# Revit family: CAF_DWDI_CW_DBD
name_source: partatom
category: Mechanical Equipment
units: mm (PartAtom-declared; Revit-internal decimal feet)

## family parameters
Always vertical = Yes
Cut with Voids When Loaded = No
Part Type = Normal
Room Calculation Point = No
Round Connector Dimension = Use Radius
Shared = No
Work Plane-Based = No

## types (58) — shared parameters
0 = 0"
1" = 1"
1.5 = 1 1/2"
2" = 2"
2' = 24"
3" = 3"
60 = 60.00°
Manufacturer = Loren Cook Company
Model = CAF-DWDI
ONE EIGTH = 1/8"
PLAY = 2"
URL = www.lorencook.com

## per-type parameters (varying)
- 120_CAF-DWDI_CW_DBD_CLASS_1: ((M+U+U+N+N)-((B+.25")/2))/2=3"; (A+.25")/2=6 3/16"; (B+.25")/2=8 31/32"; (D-(A+.25"))/2=15/16"; (INLET/2)+1.5"=9 1/2"; (INLET/2)+1.625"=9 9/16"; (INLET/2)-.125"=7 15/16"; (M-(B+.25")/2=1 7/16"; -(B+.25")/2=-8 31/32"; -P=-26 11/16"; A=12 1/8"; A+.25"=12 3/8"; A/2=6 1/16"; B=17 11/16"; B+.25"=17 15/16"; B/2=8 27/32"; BOTTOM=5 7/32"; C=1 7/16"; C+C=2 7/8"; C/2=23/32"; D/2=7 1/8"; D/7=1 3/16"; DB_D=20 1/16"; DB_E=9 13/16"; DB_F=23 3/8"; DB_G=9 5/8"; DB_H=1 1/16"; DB_J=23 3/8"; DB_R=11/16"; E/2=9 29/32"; G+(INLET/2)+1.625"=19 3/8"; G-(INLET/2)-1.625"=1/4"; G-(R/2)=3/16"; H-J=9 5/8"; INLET=16 1/8"; INLET/2=8 1/16"; INLET/4=4 1/32"; K=9/16"; K/2=9/32"; L=10 7/16"; M=20 13/16"; N=2 3/4"; OLD_G=9 13/16"; OLD_R=19 1/4"; OLD_R/2=9 5/8"; P=26 11/16"; S=20 1/2"; S/2=10 1/4"; T=19 1/2"; T/2=9 3/4"; Type Comments=Centrifugal Airfoil Blower Clockwise Down Blast Arrangement 3 Low Profile Class 1; U=4 5/16"; U-N=1 9/16"; V=1"; V+(D-(A+.25"))/2=1 15/16"
- 135_CAF-DWDI_CW_DBD_CLASS_1: ((M+U+U+N+N)-((B+.25")/2))/2=3"; (A+.25")/2=6 15/16"; (B+.25")/2=10 3/32"; (D-(A+.25"))/2=15/16"; (INLET/2)+1.5"=10 1/4"; (INLET/2)+1.625"=10 5/16"; (INLET/2)-.125"=8 11/16"; (M-(B+.25")/2=1 7/16"; -(B+.25")/2=-10 3/32"; -P=-28 15/16"; A=13 5/8"; A+.25"=13 7/8"; A/2=6 13/16"; B=19 15/16"; B+.25"=20 3/16"; B/2=9 31/32"; BOTTOM=5 7/8"; C=1 7/16"; C+C=2 7/8"; C/2=23/32"; D/2=7 7/8"; D/7=1 5/16"; DB_D=22 9/16"; DB_E=10 13/16"; DB_F=25 7/8"; DB_G=10 1/2"; DB_H=1 1/16"; DB_J=25 7/8"; DB_R=11/16"; E/2=11 1/32"; G+(INLET/2)+1.625"=21 1/8"; G-(INLET/2)-1.625"=1/2"; G-(R/2)=5/16"; H-J=10 13/16"; INLET=17 5/8"; INLET/2=8 13/16"; INLET/4=4 13/32"; K=9/16"; K/2=9/32"; L=11 9/16"; M=23 1/16"; N=2 3/4"; OLD_G=10 13/16"; OLD_R=21"; OLD_R/2=10 1/2"; P=28 15/16"; S=23"; S/2=11 1/2"; T=21 3/4"; T/2=10 7/8"; Type Comments=Centrifugal Airfoil Blower Clockwise Down Blast Arrangement 3 Low Profile Class 1; U=4 5/16"; U-N=1 9/16"; V=1"; V+(D-(A+.25"))/2=1 15/16"
- 150_CAF-DWDI_CW_DBD_CLASS_1: ((M+U+U+N+N)-((B+.25")/2))/2=3"; (A+.25")/2=7 3/4"; (B+.25")/2=11 1/8"; (D-(A+.25"))/2=15/16"; (INLET/2)+1.5"=11"; (INLET/2)+1.625"=11 1/16"; (INLET/2)-.125"=9 7/16"; (M-(B+.25")/2=1 15/16"; -(B+.25")/2=-11 1/8"; -P=-31 5/8"; A=15 1/4"; A+.25"=15 1/2"; A/2=7 5/8"; B=22"; B+.25"=22 1/4"; B/2=11"; BOTTOM=6 17/32"; C=1 7/16"; C+C=2 7/8"; C/2=23/32"; D/2=8 11/16"; D/7=1 7/16"; DB_D=25 1/16"; DB_E=12"; DB_F=28 7/16"; DB_G=11 1/2"; DB_H=1 1/16"; DB_J=28 3/16"; DB_R=7/8"; E/2=12 1/16"; G+(INLET/2)+1.625"=23 1/16"; G-(INLET/2)-1.625"=15/16"; G-(R/2)=3/4"; H-J=12"; INLET=19 1/8"; INLET/2=9 9/16"; INLET/4=4 25/32"; K=9/16"; K/2=9/32"; L=13 1/16"; M=26 1/8"; N=3 3/8"; OLD_G=12"; OLD_R=22 1/2"; OLD_R/2=11 1/4"; P=31 5/8"; S=24 15/16"; S/2=12 15/32"; T=24 3/8"; T/2=12 3/16"; Type Comments=Centrifugal Airfoil Blower Clockwise Down Blast Arrangement 3 Low Profile Class 1; U=4 7/16"; U-N=1 1/16"; V=1"; V+(D-(A+.25"))/2=1 15/16"
- 165_CAF-DWDI_CW_DBD_CLASS_1: ((M+U+U+N+N)-((B+.25")/2))/2=3"; (A+.25")/2=8 19/32"; (B+.25")/2=12 1/8"; (D-(A+.25"))/2=15/16"; (INLET/2)+1.5"=12 1/32"; (INLET/2)+1.625"=12 3/32"; (INLET/2)-.125"=10 15/32"; (M-(B+.25")/2=1 15/16"; -(B+.25")/2=-12 1/8"; -P=-33 11/16"; A=16 15/16"; A+.25"=17 3/16"; A/2=8 15/32"; B=24"; B+.25"=24 1/4"; B/2=12"; BOTTOM=7 3/16"; C=1 11/16"; C+C=3 3/8"; C/2=27/32"; D/2=9 17/32"; D/7=1 19/32"; DB_D=27 1/2"; DB_E=13 1/8"; DB_F=31 3/16"; DB_G=12 11/16"; DB_H=1 1/16"; DB_J=30 5/8"; DB_R=7/8"; E/2=13 1/16"; G+(INLET/2)+1.625"=25 7/32"; G-(INLET/2)-1.625"=1 1/32"; G-(R/2)=1"; H-J=13 1/8"; INLET=21 3/16"; INLET/2=10 19/32"; INLET/4=5 5/16"; K=15/16"; K/2=15/32"; L=14 1/16"; M=28 1/8"; N=3 3/8"; OLD_G=13 1/8"; OLD_R=24 1/4"; OLD_R/2=12 1/8"; P=33 11/16"; S=27 3/8"; S/2=13 11/16"; T=26 3/8"; T/2=13 3/16"; Type Comments=Centrifugal Airfoil Blower Clockwise Down Blast Arrangement 3 Low Profile Class 1; U=4 7/16"; U-N=1 1/16"; V=1"; V+(D-(A+.25"))/2=1 15/16"
- 180_CAF-DWDI_CW_DBD_CLASS_1: ((M+U+U+N+N)-((B+.25")/2))/2=3"; (A+.25")/2=9 3/8"; (B+.25")/2=13 5/32"; (D-(A+.25"))/2=15/16"; (INLET/2)+1.5"=12 25/32"; (INLET/2)+1.625"=12 27/32"; (INLET/2)-.125"=11 7/32"; (M-(B+.25")/2=1 15/16"; -(B+.25")/2=-13 5/32"; -P=-36 1/8"; A=18 1/2"; A+.25"=18 3/4"; A/2=9 1/4"; B=26 1/16"; B+.25"=26 5/16"; B/2=13 1/32"; BOTTOM=7 27/32"; C=1 11/16"; C+C=3 3/8"; C/2=27/32"; D/2=10 5/16"; D/7=1 23/32"; DB_D=30"; DB_E=14 5/16"; DB_F=33 15/16"; DB_G=13 13/16"; DB_H=1 1/16"; DB_J=33 1/2"; DB_R=7/8"; E/2=14 3/32"; G+(INLET/2)+1.625"=27 5/32"; G-(INLET/2)-1.625"=1 15/32"; G-(R/2)=15/16"; H-J=14 5/16"; INLET=22 11/16"; INLET/2=11 11/32"; INLET/4=5 11/16"; K=15/16"; K/2=15/32"; L=15 1/8"; M=30 3/16"; N=3 3/4"; OLD_G=14 5/16"; OLD_R=26 3/4"; OLD_R/2=13 3/8"; P=36 1/8"; S=29 3/4"; S/2=14 7/8"; T=28 7/16"; T/2=14 7/32"; Type Comments=Centrifugal Airfoil Blower Clockwise Down Blast Arrangement 3 Low Profile Class 1; U=4 13/16"; U-N=1 1/16"; V=1"; V+(D-(A+.25"))/2=1 15/16"
- 195_CAF-DWDI_CW_DBD_CLASS_1: ((M+U+U+N+N)-((B+.25")/2))/2=3"; (A+.25")/2=9 7/8"; (B+.25")/2=14 11/32"; (D-(A+.25"))/2=31/32"; (INLET/2)+1.5"=13 17/32"; (INLET/2)+1.625"=13 19/32"; (INLET/2)-.125"=11 31/32"; (M-(B+.25")/2=1 15/16"; -(B+.25")/2=-14 11/32"; -P=-38 1/2"; A=19 1/2"; A+.25"=19 3/4"; A/2=9 3/4"; B=28 7/16"; B+.25"=28 11/16"; B/2=14 7/32"; BOTTOM=8 15/32"; C=1 11/16"; C+C=3 3/8"; C/2=27/32"; D/2=10 27/32"; D/7=1 13/16"; DB_D=32 7/16"; DB_E=15 1/2"; DB_F=36 5/8"; DB_G=14 15/16"; DB_H=1 1/16"; DB_J=35 15/16"; DB_R=7/8"; E/2=15 5/16"; G+(INLET/2)+1.625"=29 3/32"; G-(INLET/2)-1.625"=1 29/32"; G-(R/2)=1 1/4"; H-J=15 1/2"; INLET=24 3/16"; INLET/2=12 3/32"; INLET/4=6 1/16"; K=15/16"; K/2=15/32"; L=16 5/16"; M=32 9/16"; N=3 3/4"; OLD_G=15 1/2"; OLD_R=28 1/2"; OLD_R/2=14 1/4"; P=38 1/2"; S=32 3/16"; S/2=16 3/32"; T=30 13/16"; T/2=15 13/32"; Type Comments=Centrifugal Airfoil Blower Clockwise Down Blast Arrangement 3 Low Profile Class 1; U=4 13/16"; U-N=1 1/16"; V=1"; V+(D-(A+.25"))/2=1 31/32"
- 210_CAF-DWDI_CW_DBD_CLASS_1: ((M+U+U+N+N)-((B+.25")/2))/2=4"; (A+.25")/2=10 15/16"; (B+.25")/2=15 5/16"; (D-(A+.25"))/2=31/32"; (INLET/2)+1.5"=14 13/32"; (INLET/2)+1.625"=14 15/32"; (INLET/2)-.125"=12 27/32"; (M-(B+.25")/2=1 15/16"; -(B+.25")/2=-15 5/16"; -P=-41 7/16"; A=21 5/8"; A+.25"=21 7/8"; A/2=10 13/16"; B=30 3/8"; B+.25"=30 5/8"; B/2=15 3/16"; BOTTOM=9 1/8"; C=1 11/16"; C+C=3 3/8"; C/2=27/32"; D/2=11 29/32"; D/7=2"; DB_D=34 15/16"; DB_E=16 11/16"; DB_F=39 3/8"; DB_G=16 1/8"; DB_H=1 1/16"; DB_J=38 5/16"; DB_R=7/8"; E/2=16 9/32"; G+(INLET/2)+1.625"=31 5/32"; G-(INLET/2)-1.625"=2 7/32"; G-(R/2)=1 11/16"; H-J=16 11/16"; INLET=25 15/16"; INLET/2=12 31/32"; INLET/4=6 1/2"; K=15/16"; K/2=15/32"; L=17 1/4"; M=34 1/2"; N=3 3/4"; OLD_G=16 11/16"; OLD_R=30"; OLD_R/2=15"; P=41 7/16"; S=34 9/16"; S/2=17 9/32"; T=32 3/4"; T/2=16 3/8"; Type Comments=Centrifugal Airfoil Blower Clockwise Down Blast Arrangement 3 Low Profile Class 1; U=5 13/16"; U-N=2 1/16"; V=1"; V+(D-(A+.25"))/2=1 31/32"
- 225_CAF-DWDI_CW_DBD_CLASS_1: ((M+U+U+N+N)-((B+.25")/2))/2=4"; (A+.25")/2=11 23/32"; (B+.25")/2=16 3/8"; (D-(A+.25"))/2=1 15/32"; (INLET/2)+1.5"=15 5/32"; (INLET/2)+1.625"=15 7/32"; (INLET/2)-.125"=13 19/32"; (M-(B+.25")/2=1 15/16"; -(B+.25")/2=-16 3/8"; -P=-44 1/16"; A=23 3/16"; A+.25"=23 7/16"; A/2=11 19/32"; B=32 1/2"; B+.25"=32 3/4"; B/2=16 1/4"; BOTTOM=9 25/32"; C=1 15/16"; C+C=3 7/8"; C/2=31/32"; D/2=13 3/16"; D/7=2 3/16"; DB_D=37 3/8"; DB_E=17 13/16"; DB_F=42 5/8"; DB_G=17 1/4"; DB_H=1 9/16"; DB_J=41 1/4"; DB_R=7/8"; E/2=17 27/32"; G+(INLET/2)+1.625"=33 1/32"; G-(INLET/2)-1.625"=2 19/32"; G-(R/2)=1 15/16"; H-J=17 13/16"; INLET=27 7/16"; INLET/2=13 23/32"; INLET/4=6 7/8"; K=15/16"; K/2=15/32"; L=18 5/16"; M=36 5/8"; N=4 1/4"; OLD_G=17 13/16"; OLD_R=31 3/4"; OLD_R/2=15 7/8"; P=44 1/16"; S=37 1/2"; S/2=18 3/4"; T=34 7/8"; T/2=17 7/16"; Type Comments=Centrifugal Airfoil Blower Clockwise Down Blast Arrangement 3 Low Profile Class 1; U=6 5/16"; U-N=2 1/16"; V=1"; V+(D-(A+.25"))/2=2 15/32"
- 245_CAF-DWDI_CW_DBD_CLASS_1: ((M+U+U+N+N)-((B+.25")/2))/2=4"; (A+.25")/2=12 7/8"; (B+.25")/2=17 21/32"; (D-(A+.25"))/2=1 15/32"; (INLET/2)+1.5"=16 5/32"; (INLET/2)+1.625"=16 7/32"; (INLET/2)-.125"=14 19/32"; (M-(B+.25")/2=1 15/16"; -(B+.25")/2=-17 21/32"; -P=-46 5/8"; A=25 1/2"; A+.25"=25 3/4"; A/2=12 3/4"; B=35 1/16"; B+.25"=35 5/16"; B/2=17 17/32"; BOTTOM=10 21/32"; C=1 15/16"; C+C=3 7/8"; C/2=31/32"; D/2=14 11/32"; D/7=2 13/32"; DB_D=40 11/16"; DB_E=19 3/8"; DB_F=46 1/4"; DB_G=18 3/4"; DB_H=1 9/16"; DB_J=44 3/8"; DB_R=7/8"; E/2=19 1/8"; G+(INLET/2)+1.625"=35 19/32"; G-(INLET/2)-1.625"=3 5/32"; G-(R/2)=2 1/2"; H-J=19 3/8"; INLET=29 7/16"; INLET/2=14 23/32"; INLET/4=7 3/8"; K=15/16"; K/2=15/32"; L=19 5/8"; M=39 3/16"; N=4 1/4"; OLD_G=19 3/8"; OLD_R=33 3/4"; OLD_R/2=16 7/8"; P=46 5/8"; S=40 5/8"; S/2=20 5/16"; T=37 7/16"; T/2=18 23/32"; Type Comments=Centrifugal Airfoil Blower Clockwise Down Blast Arrangement 3 Low Profile Class 1; U=6 5/16"; U-N=2 1/16"; V=1"; V+(D-(A+.25"))/2=2 15/32"
- 270_CAF-DWDI_CW_DBD_CLASS_1: ((M+U+U+N+N)-((B+.25")/2))/2=4 1/2"; (A+.25")/2=13 7/8"; (B+.25")/2=19 27/32"; (D-(A+.25"))/2=1 15/32"; (INLET/2)+1.5"=17 13/32"; (INLET/2)+1.625"=17 15/32"; (INLET/2)-.125"=15 27/32"; (M-(B+.25")/2=2 7/16"; -(B+.25")/2=-19 27/32"; -P=-51 1/2"; A=27 1/2"; A+.25"=27 3/4"; A/2=13 3/4"; B=39 7/16"; B+.25"=39 11/16"; B/2=19 23/32"; BOTTOM=11 3/4"; C=2 3/16"; C+C=4 3/8"; C/2=1 3/32"; D/2=15 11/32"; D/7=2 9/16"; DB_D=44 13/16"; DB_E=21 5/16"; DB_F=50 13/16"; DB_G=20 11/16"; DB_H=1 9/16"; DB_J=48 7/8"; DB_R=1 1/8"; E/2=21 5/16"; G+(INLET/2)+1.625"=38 25/32"; G-(INLET/2)-1.625"=3 27/32"; G-(R/2)=2 9/16"; H-J=21 5/16"; INLET=31 15/16"; INLET/2=15 31/32"; INLET/4=8"; K=15/16"; K/2=15/32"; L=22 5/16"; M=44 9/16"; N=4 1/4"; OLD_G=21 5/16"; OLD_R=37 1/2"; OLD_R/2=18 3/4"; P=51 1/2"; S=44 1/8"; S/2=22 1/16"; T=42 5/16"; T/2=21 5/32"; Type Comments=Centrifugal Airfoil Blower Clockwise Down Blast Arrangement 3 Low Profile Class 1; U=6 5/16"; U-N=2 1/16"; V=1"; V+(D-(A+.25"))/2=2 15/32"
- 300_CAF-DWDI_CW_DBD_CLASS_1: ((M+U+U+N+N)-((B+.25")/2))/2=4 9/16"; (A+.25")/2=15 23/32"; (B+.25")/2=21 5/8"; (D-(A+.25"))/2=1 15/32"; (INLET/2)+1.5"=18 29/32"; (INLET/2)+1.625"=18 31/32"; (INLET/2)-.125"=17 11/32"; (M-(B+.25")/2=2 7/16"; -(B+.25")/2=-21 5/8"; -P=-55 1/8"; A=31 3/16"; A+.25"=31 7/16"; A/2=15 19/32"; B=43"; B+.25"=43 1/4"; B/2=21 1/2"; BOTTOM=13 1/32"; C=2 3/16"; C+C=4 3/8"; C/2=1 3/32"; D/2=17 3/16"; D/7=2 7/8"; DB_D=49 3/4"; DB_E=23 11/16"; DB_F=56 1/4"; DB_G=22 15/16"; DB_H=1 9/16"; DB_J=53 9/16"; DB_R=1 1/8"; E/2=23 3/32"; G+(INLET/2)+1.625"=42 21/32"; G-(INLET/2)-1.625"=4 23/32"; G-(R/2)=3 7/16"; H-J=23 11/16"; INLET=34 15/16"; INLET/2=17 15/32"; INLET/4=8 3/4"; K=15/16"; K/2=15/32"; L=24 1/16"; M=48 1/8"; N=4 1/4"; OLD_G=23 11/16"; OLD_R=40 1/2"; OLD_R/2=20 1/4"; P=55 1/8"; S=48 13/16"; S/2=24 13/32"; T=45 7/8"; T/2=22 15/16"; Type Comments=Centrifugal Airfoil Blower Clockwise Down Blast Arrangement 3 Low Profile Class 1; U=6 3/8"; U-N=2 1/8"; V=1"; V+(D-(A+.25"))/2=2 15/32"
- 330_CAF-DWDI_CW_DBD_CLASS_1: ((M+U+U+N+N)-((B+.25")/2))/2=4 9/16"; (A+.25")/2=17 3/8"; (B+.25")/2=23 21/32"; (D-(A+.25"))/2=2"; (INLET/2)+1.5"=20 13/32"; (INLET/2)+1.625"=20 15/32"; (INLET/2)-.125"=18 27/32"; (M-(B+.25")/2=2 15/16"; -(B+.25")/2=-23 21/32"; -P=-59 5/16"; A=34 1/2"; A+.25"=34 3/4"; A/2=17 1/4"; B=47 1/16"; B+.25"=47 5/16"; B/2=23 17/32"; BOTTOM=14 11/32"; C=2 7/16"; C+C=4 7/8"; C/2=1 7/32"; D/2=19 3/8"; D/7=3 7/32"; DB_D=54 11/16"; DB_E=26"; DB_F=62 1/4"; DB_G=25 1/4"; DB_H=2 1/16"; DB_J=57 13/16"; DB_R=1 5/16"; E/2=25 21/32"; G+(INLET/2)+1.625"=46 15/32"; G-(INLET/2)-1.625"=5 17/32"; G-(R/2)=5 7/32"; H-J=26"; INLET=37 15/16"; INLET/2=18 31/32"; INLET/4=9 1/2"; K=15/16"; K/2=15/32"; L=26 5/8"; M=53 3/16"; N=4 3/8"; OLD_G=26"; OLD_R=41 9/16"; OLD_R/2=20 25/32"; P=59 5/16"; S=53 3/4"; S/2=26 7/8"; T=50 9/16"; T/2=25 9/32"; Type Comments=Centrifugal Airfoil Blower Clockwise Down Blast Arrangement 3 Low Profile Class 1; U=6"; U-N=1 5/8"; V=1"; V+(D-(A+.25"))/2=3"
- 365_CAF-DWDI_CW_DBD_CLASS_1: ((M+U+U+N+N)-((B+.25")/2))/2=5 1/16"; (A+.25")/2=19 15/32"; (B+.25")/2=26 7/32"; (D-(A+.25"))/2=2"; (INLET/2)+1.5"=22 5/32"; (INLET/2)+1.625"=22 7/32"; (INLET/2)-.125"=20 19/32"; (M-(B+.25")/2=2 15/16"; -(B+.25")/2=-26 7/32"; -P=-65 5/16"; A=38 11/16"; A+.25"=38 15/16"; A/2=19 11/32"; B=52 3/16"; B+.25"=52 7/16"; B/2=26 3/32"; BOTTOM=15 7/8"; C=2 11/16"; C+C=5 3/8"; C/2=1 11/32"; D/2=21 15/32"; D/7=3 19/32"; DB_D=60 1/2"; DB_E=28 3/4"; DB_F=68 5/8"; DB_G=27 15/16"; DB_H=2 1/16"; DB_J=63 3/8"; DB_R=1 5/16"; E/2=28 7/32"; G+(INLET/2)+1.625"=50 31/32"; G-(INLET/2)-1.625"=6 17/32"; G-(R/2)=6 3/32"; H-J=28 3/4"; INLET=41 7/16"; INLET/2=20 23/32"; INLET/4=10 3/8"; K=15/16"; K/2=15/32"; L=29 3/16"; M=58 5/16"; N=4 3/4"; OLD_G=28 3/4"; OLD_R=45 5/16"; OLD_R/2=22 21/32"; P=65 5/16"; S=59 5/16"; S/2=29 21/32"; T=55 11/16"; T/2=27 27/32"; Type Comments=Centrifugal Airfoil Blower Clockwise Down Blast Arrangement 3 Low Profile Class 1; U=6 7/8"; U-N=2 1/8"; V=1"; V+(D-(A+.25"))/2=3"
- 402_CAF-DWDI_CW_DBD_CLASS_1: ((M+U+U+N+N)-((B+.25")/2))/2=5 1/16"; (A+.25")/2=21"; (B+.25")/2=29 1/32"; (D-(A+.25"))/2=2 1/32"; (INLET/2)+1.5"=24 1/32"; (INLET/2)+1.625"=24 3/32"; (INLET/2)-.125"=22 15/32"; (M-(B+.25")/2=3 15/16"; -(B+.25")/2=-29 1/32"; -P=-71 15/16"; A=41 3/4"; A+.25"=42"; A/2=20 7/8"; B=57 13/16"; B+.25"=58 1/16"; B/2=28 29/32"; BOTTOM=17 15/32"; C=2 15/16"; C+C=5 7/8"; C/2=1 15/32"; D/2=23 1/32"; D/7=3 27/32"; DB_D=66 9/16"; DB_E=31 11/16"; DB_F=75 3/8"; DB_G=30 3/4"; DB_H=2 1/16"; DB_J=69 7/16"; DB_R=1 3/4"; E/2=31"; G+(INLET/2)+1.625"=55 25/32"; G-(INLET/2)-1.625"=7 19/32"; G-(R/2)=6 27/32"; H-J=31 5/8"; INLET=45 3/16"; INLET/2=22 19/32"; INLET/4=11 5/16"; K=15/16"; K/2=15/32"; L=33"; M=65 15/16"; N=4 7/8"; OLD_G=31 11/16"; OLD_R=49 11/16"; OLD_R/2=24 27/32"; P=71 15/16"; S=64 3/8"; S/2=32 3/16"; T=62 7/16"; T/2=31 7/32"; Type Comments=Centrifugal Airfoil Blower Clockwise Down Blast Arrangement 3 Low Profile Class 1; U=6"; U-N=1 1/8"; V=1 15/16"; V+(D-(A+.25"))/2=3 31/32"
- 445_CAF-DWDI_CW_DBD_CLASS_1: ((M+U+U+N+N)-((B+.25")/2))/2=5 3/32"; (A+.25")/2=23 3/32"; (B+.25")/2=32 1/4"; (D-(A+.25"))/2=2 1/16"; (INLET/2)+1.5"=26 5/32"; (INLET/2)+1.625"=26 7/32"; (INLET/2)-.125"=24 19/32"; (M-(B+.25")/2=3 31/32"; -(B+.25")/2=-32 1/4"; -P=-79 5/16"; A=45 15/16"; A+.25"=46 3/16"; A/2=22 31/32"; B=64 1/4"; B+.25"=64 1/2"; B/2=32 1/8"; BOTTOM=19 11/32"; C=2 15/16"; C+C=5 7/8"; C/2=1 15/32"; D/2=25 5/32"; D/7=4 3/16"; DB_D=73 11/16"; DB_E=35"; DB_F=83 1/4"; DB_G=34 1/16"; DB_H=2 1/8"; DB_J=76 3/16"; DB_R=1 3/4"; E/2=34 9/32"; G+(INLET/2)+1.625"=61 7/32"; G-(INLET/2)-1.625"=8 25/32"; G-(R/2)=8 1/32"; H-J=35"; INLET=49 7/16"; INLET/2=24 23/32"; INLET/4=12 3/8"; K=1 1/16"; K/2=17/32"; L=36 1/4"; M=72 7/16"; N=5 3/4"; OLD_G=35"; OLD_R=53 15/16"; OLD_R/2=26 31/32"; P=79 5/16"; S=71 1/16"; S/2=35 17/32"; T=68 15/16"; T/2=34 15/32"; Type Comments=Centrifugal Airfoil Blower Clockwise Down Blast Arrangement 3 Low Profile Class 1; U=6 7/8"; U-N=1 1/8"; V=1 15/16"; V+(D-(A+.25"))/2=4"
- 490_CAF-DWDI_CW_DBD_CLASS_1: ((M+U+U+N+N)-((B+.25")/2))/2=5 3/32"; (A+.25")/2=25 5/8"; (B+.25")/2=35 3/16"; (D-(A+.25"))/2=2 1/16"; (INLET/2)+1.5"=28 15/16"; (INLET/2)+1.625"=29"; (INLET/2)-.125"=27 3/8"; (M-(B+.25")/2=3 31/32"; -(B+.25")/2=-35 3/16"; -P=-85 5/16"; A=51"; A+.25"=51 1/4"; A/2=25 1/2"; B=70 1/8"; B+.25"=70 3/8"; B/2=35 1/16"; BOTTOM=21 9/32"; C=3 7/16"; C+C=6 7/8"; C/2=1 23/32"; D/2=27 11/16"; D/7=4 5/8"; DB_D=81 1/8"; DB_E=38 9/16"; DB_F=91 7/16"; DB_G=37 1/2"; DB_H=2 1/8"; DB_J=83 5/16"; DB_R=1 3/4"; E/2=37 7/32"; G+(INLET/2)+1.625"=67 9/16"; G-(INLET/2)-1.625"=9 9/16"; G-(R/2)=9 7/32"; H-J=38 9/16"; INLET=55"; INLET/2=27 1/2"; INLET/4=13 3/4"; K=1 1/16"; K/2=17/32"; L=39 3/16"; M=78 5/16"; N=5 7/8"; OLD_G=38 9/16"; OLD_R=58 11/16"; OLD_R/2=29 11/32"; P=85 5/16"; S=78 3/16"; S/2=39 3/32"; T=74 13/16"; T/2=37 13/32"; Type Comments=Centrifugal Airfoil Blower Clockwise Down Blast Arrangement 3 Low Profile Class 1; U=7"; U-N=1 1/8"; V=1 15/16"; V+(D-(A+.25"))/2=4"
- 540_CAF-DWDI_CW_DBD_CLASS_1: ((M+U+U+N+N)-((B+.25")/2))/2=5 3/32"; (A+.25")/2=28"; (B+.25")/2=39 3/32"; (D-(A+.25"))/2=2 1/16"; (INLET/2)+1.5"=31 7/16"; (INLET/2)+1.625"=31 1/2"; (INLET/2)-.125"=29 7/8"; (M-(B+.25")/2=3 31/32"; -(B+.25")/2=-39 3/32"; -P=-93 1/2"; A=55 3/4"; A+.25"=56"; A/2=27 7/8"; B=77 15/16"; B+.25"=78 3/16"; B/2=38 31/32"; BOTTOM=23 15/32"; C=2 15/16"; C+C=5 7/8"; C/2=1 15/32"; D/2=30 1/16"; D/7=5"; DB_D=89 3/8"; DB_E=42 7/16"; DB_F=100 9/16"; DB_G=41 5/16"; DB_H=2 1/8"; DB_J=91 1/16"; DB_R=1 3/4"; E/2=41 3/32"; G+(INLET/2)+1.625"=73 15/16"; G-(INLET/2)-1.625"=10 15/16"; G-(R/2)=10 19/32"; H-J=42 7/16"; INLET=60"; INLET/2=30"; INLET/4=15"; K=1 1/16"; K/2=17/32"; L=43 1/16"; M=86 1/8"; N=6 1/4"; OLD_G=42 7/16"; OLD_R=63 11/16"; OLD_R/2=31 27/32"; P=93 1/2"; S=86"; S/2=43"; T=82 5/8"; T/2=41 5/16"; Type Comments=Centrifugal Airfoil Blower Clockwise Down Blast Arrangement 3 Low Profile Class 1; U=7 3/8"; U-N=1 1/8"; V=1 15/16"; V+(D-(A+.25"))/2=4"
- 600_CAF-DWDI_CW_DBD_CLASS_1: ((M+U+U+N+N)-((B+.25")/2))/2=5 1/8"; (A+.25")/2=31 7/32"; (B+.25")/2=43 1/4"; (D-(A+.25"))/2=2 1/16"; (INLET/2)+1.5"=34 7/16"; (INLET/2)+1.625"=34 1/2"; (INLET/2)-.125"=32 7/8"; (M-(B+.25")/2=5"; -(B+.25")/2=-43 1/4"; -P=-102 7/8"; A=62 3/16"; A+.25"=62 7/16"; A/2=31 3/32"; B=86 1/4"; B+.25"=86 1/2"; B/2=43 1/8"; BOTTOM=26 3/32"; C=2 15/16"; C+C=5 7/8"; C/2=1 15/32"; D/2=33 9/32"; D/7=5 9/16"; DB_D=99 5/16"; DB_E=47 1/8"; DB_F=111 9/16"; DB_G=45 15/16"; DB_H=2 1/8"; DB_J=100 5/8"; DB_R=2 1/4"; E/2=45 9/32"; G+(INLET/2)+1.625"=81 5/8"; G-(INLET/2)-1.625"=12 5/8"; G-(R/2)=12 1/8"; H-J=47 1/8"; INLET=66"; INLET/2=33"; INLET/4=16 1/2"; K=1 1/16"; K/2=17/32"; L=48 1/4"; M=96 1/2"; N=6 1/4"; OLD_G=47 1/8"; OLD_R=70"; OLD_R/2=35"; P=102 7/8"; S=94 3/8"; S/2=47 3/16"; T=92"; T/2=46"; Type Comments=Centrifugal Airfoil Blower Clockwise Down Blast Arrangement 3 Low Profile Class 1; U=6 3/8"; U-N=1/8"; V=2 15/16"; V+(D-(A+.25"))/2=5"
- 660_CAF-DWDI_CW_DBD_CLASS_1: ((M+U+U+N+N)-((B+.25")/2))/2=6 5/8"; (A+.25")/2=34 11/32"; (B+.25")/2=47 9/16"; (D-(A+.25"))/2=2 1/16"; (INLET/2)+1.5"=37 7/16"; (INLET/2)+1.625"=37 1/2"; (INLET/2)-.125"=35 7/8"; (M-(B+.25")/2=6"; -(B+.25")/2=-47 9/16"; -P=-117 1/8"; A=68 7/16"; A+.25"=68 11/16"; A/2=34 7/32"; B=94 7/8"; B+.25"=95 1/8"; B/2=47 7/16"; BOTTOM=28 11/16"; C=3 7/16"; C+C=6 7/8"; C/2=1 23/32"; D/2=36 13/32"; D/7=6 1/16"; DB_D=109 3/16"; DB_E=51 13/16"; DB_F=122 1/2"; DB_G=50 1/2"; DB_H=2 1/8"; DB_J=110 1/4"; DB_R=2 3/4"; E/2=49 5/8"; G+(INLET/2)+1.625"=89 5/16"; G-(INLET/2)-1.625"=14 5/16"; G-(R/2)=13 17/32"; H-J=51 13/16"; INLET=72"; INLET/2=36"; INLET/4=18"; K=1 1/16"; K/2=17/32"; L=53 9/16"; M=107 1/8"; N=9 3/8"; OLD_G=51 13/16"; OLD_R=76 9/16"; OLD_R/2=38 9/32"; P=117 1/8"; S=102 3/4"; S/2=51 3/8"; T=101 5/8"; T/2=50 13/16"; Type Comments=Centrifugal Airfoil Blower Clockwise Down Blast Arrangement 3 Low Profile Class 1; U=10"; U-N=5/8"; V=3 15/16"; V+(D-(A+.25"))/2=6"
- 730_CAF-DWDI_CW_DBD_CLASS_1: ((M+U+U+N+N)-((B+.25")/2))/2=6 5/8"; (A+.25")/2=38 1/32"; (B+.25")/2=52 1/2"; (D-(A+.25"))/2=2 9/16"; (INLET/2)+1.5"=40 15/16"; (INLET/2)+1.625"=41"; (INLET/2)-.125"=39 3/8"; (M-(B+.25")/2=6"; -(B+.25")/2=-52 1/2"; -P=-127"; A=75 13/16"; A+.25"=76 1/16"; A/2=37 29/32"; B=104 3/4"; B+.25"=105"; B/2=52 3/8"; BOTTOM=31 23/32"; C=3 7/16"; C+C=6 7/8"; C/2=1 23/32"; D/2=40 19/32"; D/7=6 25/32"; DB_D=120 11/16"; DB_E=57 5/16"; DB_F=135 3/4"; DB_G=55 13/16"; DB_H=2 5/8"; DB_J=121 11/16"; DB_R=2 3/4"; E/2=55 1/16"; G+(INLET/2)+1.625"=98 5/16"; G-(INLET/2)-1.625"=16 5/16"; G-(R/2)=15 17/32"; H-J=57 1/4"; INLET=79"; INLET/2=39 1/2"; INLET/4=19 3/4"; K=1 1/16"; K/2=17/32"; L=58 1/2"; M=117"; N=9 3/8"; OLD_G=57 5/16"; OLD_R=83 9/16"; OLD_R/2=41 25/32"; P=127"; S=114 1/8"; S/2=57 1/16"; T=111 1/2"; T/2=55 3/4"; Type Comments=Centrifugal Airfoil Blower Clockwise Down Blast Arrangement 3 Low Profile Class 1; U=10"; U-N=5/8"; V=3 7/16"; V+(D-(A+.25"))/2=6"
- 120_CAF-DWDI_CW_DBD_CLASS_2: ((M+U+U+N+N)-((B+.25")/2))/2=3 1/2"; (A+.25")/2=6 3/16"; (B+.25")/2=8 31/32"; (D-(A+.25"))/2=15/16"; (INLET/2)+1.5"=9 1/2"; (INLET/2)+1.625"=9 9/16"; (INLET/2)-.125"=7 15/16"; (M-(B+.25")/2=1 15/16"; -(B+.25")/2=-8 31/32"; -P=-28 3/16"; A=12 1/8"; A+.25"=12 3/8"; A/2=6 1/16"; B=17 11/16"; B+.25"=17 15/16"; B/2=8 27/32"; BOTTOM=5 7/32"; C=1 7/16"; C+C=2 7/8"; C/2=23/32"; D/2=7 1/8"; D/7=1 3/16"; DB_D=20 1/16"; DB_E=9 13/16"; DB_F=23 3/8"; DB_G=9 5/8"; DB_H=1 1/16"; DB_J=23 3/8"; DB_R=7/8"; E/2=9 29/32"; G+(INLET/2)+1.625"=19 3/8"; G-(INLET/2)-1.625"=1/4"; G-(R/2)=3/16"; H-J=9 5/8"; INLET=16 1/8"; INLET/2=8 1/16"; INLET/4=4 1/32"; K=15/16"; K/2=15/32"; L=10 15/16"; M=21 13/16"; N=3 3/4"; OLD_G=9 13/16"; OLD_R=19 1/4"; OLD_R/2=9 5/8"; P=28 3/16"; S=20 1/8"; S/2=10 1/16"; T=20 1/16"; T/2=10 1/32"; Type Comments=Centrifugal Airfoil Blower Clockwise Down Blast Arrangement 3 Low Profile Class 2; U=5 5/16"; U-N=1 9/16"; V=1"; V+(D-(A+.25"))/2=1 15/16"
- 135_CAF-DWDI_CW_DBD_CLASS_2: ((M+U+U+N+N)-((B+.25")/2))/2=3 1/2"; (A+.25")/2=6 15/16"; (B+.25")/2=10 3/32"; (D-(A+.25"))/2=15/16"; (INLET/2)+1.5"=10 1/4"; (INLET/2)+1.625"=10 5/16"; (INLET/2)-.125"=8 11/16"; (M-(B+.25")/2=1 15/16"; -(B+.25")/2=-10 3/32"; -P=-30 9/16"; A=13 5/8"; A+.25"=13 7/8"; A/2=6 13/16"; B=19 15/16"; B+.25"=20 3/16"; B/2=9 31/32"; BOTTOM=5 7/8"; C=1 7/16"; C+C=2 7/8"; C/2=23/32"; D/2=7 7/8"; D/7=1 5/16"; DB_D=22 9/16"; DB_E=10 13/16"; DB_F=25 7/8"; DB_G=10 1/2"; DB_H=1 1/16"; DB_J=25 7/8"; DB_R=7/8"; E/2=11 1/32"; G+(INLET/2)+1.625"=21 1/8"; G-(INLET/2)-1.625"=1/2"; G-(R/2)=5/16"; H-J=10 13/16"; INLET=17 5/8"; INLET/2=8 13/16"; INLET/4=4 13/32"; K=15/16"; K/2=15/32"; L=12 1/16"; M=24 1/16"; N=3 7/8"; OLD_G=10 13/16"; OLD_R=21"; OLD_R/2=10 1/2"; P=30 9/16"; S=22 5/8"; S/2=11 5/16"; T=22 5/16"; T/2=11 5/32"; Type Comments=Centrifugal Airfoil Blower Clockwise Down Blast Arrangement 3 Low Profile Class 2; U=5 7/16"; U-N=1 9/16"; V=1"; V+(D-(A+.25"))/2=1 15/16"
- 150_CAF-DWDI_CW_DBD_CLASS_2: ((M+U+U+N+N)-((B+.25")/2))/2=4"; (A+.25")/2=7 3/4"; (B+.25")/2=11 1/8"; (D-(A+.25"))/2=15/16"; (INLET/2)+1.5"=11"; (INLET/2)+1.625"=11 1/16"; (INLET/2)-.125"=9 7/16"; (M-(B+.25")/2=1 15/16"; -(B+.25")/2=-11 1/8"; -P=-33 1/8"; A=15 1/4"; A+.25"=15 1/2"; A/2=7 5/8"; B=22"; B+.25"=22 1/4"; B/2=11"; BOTTOM=6 17/32"; C=1 15/16"; C+C=3 7/8"; C/2=31/32"; D/2=8 11/16"; D/7=1 7/16"; DB_D=25 1/16"; DB_E=12"; DB_F=28 11/16"; DB_G=11 3/4"; DB_H=1 1/16"; DB_J=28 11/16"; DB_R=7/8"; E/2=12 1/16"; G+(INLET/2)+1.625"=23 1/16"; G-(INLET/2)-1.625"=15/16"; G-(R/2)=3/4"; H-J=12"; INLET=19 1/8"; INLET/2=9 9/16"; INLET/4=4 25/32"; K=15/16"; K/2=15/32"; L=13 1/16"; M=26 1/8"; N=3 7/8"; OLD_G=12"; OLD_R=22 1/2"; OLD_R/2=11 1/4"; P=33 1/8"; S=24 15/16"; S/2=12 15/32"; T=24 3/8"; T/2=12 3/16"; Type Comments=Centrifugal Airfoil Blower Clockwise Down Blast Arrangement 3 Low Profile Class 2; U=5 15/16"; U-N=2 1/16"; V=1"; V+(D-(A+.25"))/2=1 15/16"
- 165_CAF-DWDI_CW_DBD_CLASS_2: ((M+U+U+N+N)-((B+.25")/2))/2=4"; (A+.25")/2=8 19/32"; (B+.25")/2=12 1/8"; (D-(A+.25"))/2=15/16"; (INLET/2)+1.5"=12 1/32"; (INLET/2)+1.625"=12 3/32"; (INLET/2)-.125"=10 15/32"; (M-(B+.25")/2=1 15/16"; -(B+.25")/2=-12 1/8"; -P=-35 3/16"; A=16 15/16"; A+.25"=17 3/16"; A/2=8 15/32"; B=24"; B+.25"=24 1/4"; B/2=12"; BOTTOM=7 3/16"; C=1 15/16"; C+C=3 7/8"; C/2=31/32"; D/2=9 17/32"; D/7=1 19/32"; DB_D=27 1/2"; DB_E=13 1/8"; DB_F=31 3/16"; DB_G=12 11/16"; DB_H=1 1/16"; DB_J=31 1/8"; DB_R=7/8"; E/2=13 1/16"; G+(INLET/2)+1.625"=25 7/32"; G-(INLET/2)-1.625"=1 1/32"; G-(R/2)=1"; H-J=13 1/8"; INLET=21 3/16"; INLET/2=10 19/32"; INLET/4=5 5/16"; K=15/16"; K/2=15/32"; L=14 1/16"; M=28 1/8"; N=3 7/8"; OLD_G=13 1/8"; OLD_R=24 1/4"; OLD_R/2=12 1/8"; P=35 3/16"; S=27 3/8"; S/2=13 11/16"; T=26 3/8"; T/2=13 3/16"; Type Comments=Centrifugal Airfoil Blower Clockwise Down Blast Arrangement 3 Low Profile Class 2; U=5 15/16"; U-N=2 1/16"; V=1"; V+(D-(A+.25"))/2=1 15/16"
- 180_CAF-DWDI_CW_DBD_CLASS_2: ((M+U+U+N+N)-((B+.25")/2))/2=4"; (A+.25")/2=9 3/8"; (B+.25")/2=13 5/32"; (D-(A+.25"))/2=15/16"; (INLET/2)+1.5"=12 25/32"; (INLET/2)+1.625"=12 27/32"; (INLET/2)-.125"=11 7/32"; (M-(B+.25")/2=1 15/16"; -(B+.25")/2=-13 5/32"; -P=-37 1/4"; A=18 1/2"; A+.25"=18 3/4"; A/2=9 1/4"; B=26 1/16"; B+.25"=26 5/16"; B/2=13 1/32"; BOTTOM=7 27/32"; C=1 15/16"; C+C=3 7/8"; C/2=31/32"; D/2=10 5/16"; D/7=1 23/32"; DB_D=30"; DB_E=14 5/16"; DB_F=33 15/16"; DB_G=13 13/16"; DB_H=1 1/16"; DB_J=33 1/2"; DB_R=7/8"; E/2=14 3/32"; G+(INLET/2)+1.625"=27 5/32"; G-(INLET/2)-1.625"=1 15/32"; G-(R/2)=15/16"; H-J=14 5/16"; INLET=22 11/16"; INLET/2=11 11/32"; INLET/4=5 11/16"; K=15/16"; K/2=15/32"; L=15 1/8"; M=30 3/16"; N=3 7/8"; OLD_G=14 5/16"; OLD_R=26 3/4"; OLD_R/2=13 3/8"; P=37 1/4"; S=29 3/4"; S/2=14 7/8"; T=28 7/16"; T/2=14 7/32"; Type Comments=Centrifugal Airfoil Blower Clockwise Down Blast Arrangement 3 Low Profile Class 2; U=5 15/16"; U-N=2 1/16"; V=1"; V+(D-(A+.25"))/2=1 15/16"
- 195_CAF-DWDI_CW_DBD_CLASS_2: ((M+U+U+N+N)-((B+.25")/2))/2=5"; (A+.25")/2=9 7/8"; (B+.25")/2=14 11/32"; (D-(A+.25"))/2=31/32"; (INLET/2)+1.5"=13 17/32"; (INLET/2)+1.625"=13 19/32"; (INLET/2)-.125"=11 31/32"; (M-(B+.25")/2=1 15/16"; -(B+.25")/2=-14 11/32"; -P=-39 5/8"; A=19 1/2"; A+.25"=19 3/4"; A/2=9 3/4"; B=28 7/16"; B+.25"=28 11/16"; B/2=14 7/32"; BOTTOM=8 15/32"; C=1 15/16"; C+C=3 7/8"; C/2=31/32"; D/2=10 27/32"; D/7=1 13/16"; DB_D=32 7/16"; DB_E=15 1/2"; DB_F=36 5/8"; DB_G=14 15/16"; DB_H=1 1/16"; DB_J=35 15/16"; DB_R=7/8"; E/2=15 5/16"; G+(INLET/2)+1.625"=29 3/32"; G-(INLET/2)-1.625"=1 29/32"; G-(R/2)=1 1/4"; H-J=15 1/2"; INLET=24 3/16"; INLET/2=12 3/32"; INLET/4=6 1/16"; K=15/16"; K/2=15/32"; L=16 5/16"; M=32 9/16"; N=3 7/8"; OLD_G=15 1/2"; OLD_R=28 1/2"; OLD_R/2=14 1/4"; P=39 5/8"; S=32 3/16"; S/2=16 3/32"; T=30 13/16"; T/2=15 13/32"; Type Comments=Centrifugal Airfoil Blower Clockwise Down Blast Arrangement 3 Low Profile Class 2; U=6 15/16"; U-N=3 1/16"; V=1"; V+(D-(A+.25"))/2=1 31/32"
- 210_CAF-DWDI_CW_DBD_CLASS_2: ((M+U+U+N+N)-((B+.25")/2))/2=4 1/2"; (A+.25")/2=10 15/16"; (B+.25")/2=15 5/16"; (D-(A+.25"))/2=31/32"; (INLET/2)+1.5"=14 13/32"; (INLET/2)+1.625"=14 15/32"; (INLET/2)-.125"=12 27/32"; (M-(B+.25")/2=1 15/16"; -(B+.25")/2=-15 5/16"; -P=-42 7/16"; A=21 5/8"; A+.25"=21 7/8"; A/2=10 13/16"; B=30 3/8"; B+.25"=30 5/8"; B/2=15 3/16"; BOTTOM=9 1/8"; C=2 3/16"; C+C=4 3/8"; C/2=1 3/32"; D/2=11 29/32"; D/7=2"; DB_D=34 15/16"; DB_E=16 11/16"; DB_F=39 3/8"; DB_G=16 1/8"; DB_H=1 1/16"; DB_J=38 5/16"; DB_R=7/8"; E/2=16 9/32"; G+(INLET/2)+1.625"=31 5/32"; G-(INLET/2)-1.625"=2 7/32"; G-(R/2)=1 11/16"; H-J=16 11/16"; INLET=25 15/16"; INLET/2=12 31/32"; INLET/4=6 1/2"; K=15/16"; K/2=15/32"; L=17 1/4"; M=34 1/2"; N=4 1/4"; OLD_G=16 11/16"; OLD_R=30"; OLD_R/2=15"; P=42 7/16"; S=34 9/16"; S/2=17 9/32"; T=32 3/4"; T/2=16 3/8"; Type Comments=Centrifugal Airfoil Blower Clockwise Down Blast Arrangement 3 Low Profile Class 2; U=6 13/16"; U-N=2 9/16"; V=1"; V+(D-(A+.25"))/2=1 31/32"
- 225_CAF-DWDI_CW_DBD_CLASS_2: ((M+U+U+N+N)-((B+.25")/2))/2=4 1/2"; (A+.25")/2=11 23/32"; (B+.25")/2=16 3/8"; (D-(A+.25"))/2=1 15/32"; (INLET/2)+1.5"=15 5/32"; (INLET/2)+1.625"=15 7/32"; (INLET/2)-.125"=13 19/32"; (M-(B+.25")/2=1 15/16"; -(B+.25")/2=-16 3/8"; -P=-44 9/16"; A=23 3/16"; A+.25"=23 7/16"; A/2=11 19/32"; B=32 1/2"; B+.25"=32 3/4"; B/2=16 1/4"; BOTTOM=9 25/32"; C=2 3/16"; C+C=4 3/8"; C/2=1 3/32"; D/2=13 3/16"; D/7=2 3/16"; DB_D=37 3/8"; DB_E=17 13/16"; DB_F=42 5/8"; DB_G=17 1/4"; DB_H=1 9/16"; DB_J=41 1/4"; DB_R=7/8"; E/2=17 27/32"; G+(INLET/2)+1.625"=33 1/32"; G-(INLET/2)-1.625"=2 19/32"; G-(R/2)=1 15/16"; H-J=17 13/16"; INLET=27 7/16"; INLET/2=13 23/32"; INLET/4=6 7/8"; K=15/16"; K/2=15/32"; L=18 5/16"; M=36 5/8"; N=4 1/4"; OLD_G=17 13/16"; OLD_R=31 3/4"; OLD_R/2=15 7/8"; P=44 9/16"; S=37 1/2"; S/2=18 3/4"; T=34 7/8"; T/2=17 7/16"; Type Comments=Centrifugal Airfoil Blower Clockwise Down Blast Arrangement 3 Low Profile Class 2; U=6 13/16"; U-N=2 9/16"; V=1"; V+(D-(A+.25"))/2=2 15/32"
- 245_CAF-DWDI_CW_DBD_CLASS_2: ((M+U+U+N+N)-((B+.25")/2))/2=4 1/2"; (A+.25")/2=12 7/8"; (B+.25")/2=17 21/32"; (D-(A+.25"))/2=1 15/32"; (INLET/2)+1.5"=16 5/32"; (INLET/2)+1.625"=16 7/32"; (INLET/2)-.125"=14 19/32"; (M-(B+.25")/2=1 15/16"; -(B+.25")/2=-17 21/32"; -P=-47 1/4"; A=25 1/2"; A+.25"=25 3/4"; A/2=12 3/4"; B=35 1/16"; B+.25"=35 5/16"; B/2=17 17/32"; BOTTOM=10 21/32"; C=2 7/16"; C+C=4 7/8"; C/2=1 7/32"; D/2=14 11/32"; D/7=2 13/32"; DB_D=40 11/16"; DB_E=19 3/8"; DB_F=46 1/4"; DB_G=18 3/4"; DB_H=1 9/16"; DB_J=44 3/8"; DB_R=7/8"; E/2=19 1/8"; G+(INLET/2)+1.625"=35 19/32"; G-(INLET/2)-1.625"=3 5/32"; G-(R/2)=2 1/2"; H-J=19 3/8"; INLET=29 7/16"; INLET/2=14 23/32"; INLET/4=7 3/8"; K=15/16"; K/2=15/32"; L=19 5/8"; M=39 3/16"; N=4 3/8"; OLD_G=19 3/8"; OLD_R=33 3/4"; OLD_R/2=16 7/8"; P=47 1/4"; S=40 5/8"; S/2=20 5/16"; T=37 7/16"; T/2=18 23/32"; Type Comments=Centrifugal Airfoil Blower Clockwise Down Blast Arrangement 3 Low Profile Class 2; U=6 15/16"; U-N=2 9/16"; V=1"; V+(D-(A+.25"))/2=2 15/32"
- 270_CAF-DWDI_CW_DBD_CLASS_2: ((M+U+U+N+N)-((B+.25")/2))/2=4 1/2"; (A+.25")/2=13 7/8"; (B+.25")/2=19 27/32"; (D-(A+.25"))/2=1 15/32"; (INLET/2)+1.5"=17 13/32"; (INLET/2)+1.625"=17 15/32"; (INLET/2)-.125"=15 27/32"; (M-(B+.25")/2=2 7/16"; -(B+.25")/2=-19 27/32"; -P=-51 5/8"; A=27 1/2"; A+.25"=27 3/4"; A/2=13 3/4"; B=39 7/16"; B+.25"=39 11/16"; B/2=19 23/32"; BOTTOM=11 3/4"; C=2 7/16"; C+C=4 7/8"; C/2=1 7/32"; D/2=15 11/32"; D/7=2 9/16"; DB_D=44 13/16"; DB_E=21 5/16"; DB_F=50 13/16"; DB_G=20 11/16"; DB_H=1 9/16"; DB_J=48 7/8"; DB_R=1 1/8"; E/2=21 5/16"; G+(INLET/2)+1.625"=38 25/32"; G-(INLET/2)-1.625"=3 27/32"; G-(R/2)=2 9/16"; H-J=21 5/16"; INLET=31 15/16"; INLET/2=15 31/32"; INLET/4=8"; K=15/16"; K/2=15/32"; L=22 5/16"; M=44 9/16"; N=4 3/8"; OLD_G=21 5/16"; OLD_R=37 1/2"; OLD_R/2=18 3/4"; P=51 5/8"; S=44 1/8"; S/2=22 1/16"; T=42 5/16"; T/2=21 5/32"; Type Comments=Centrifugal Airfoil Blower Clockwise Down Blast Arrangement 3 Low Profile Class 2; U=6 7/16"; U-N=2 1/16"; V=1"; V+(D-(A+.25"))/2=2 15/32"
- 300_CAF-DWDI_CW_DBD_CLASS_2: ((M+U+U+N+N)-((B+.25")/2))/2=5 1/16"; (A+.25")/2=15 23/32"; (B+.25")/2=21 5/8"; (D-(A+.25"))/2=1 15/32"; (INLET/2)+1.5"=18 29/32"; (INLET/2)+1.625"=18 31/32"; (INLET/2)-.125"=17 11/32"; (M-(B+.25")/2=2 7/16"; -(B+.25")/2=-21 5/8"; -P=-56 1/8"; A=31 3/16"; A+.25"=31 7/16"; A/2=15 19/32"; B=43"; B+.25"=43 1/4"; B/2=21 1/2"; BOTTOM=13 1/32"; C=2 11/16"; C+C=5 3/8"; C/2=1 11/32"; D/2=17 3/16"; D/7=2 7/8"; DB_D=49 3/4"; DB_E=23 11/16"; DB_F=56 1/4"; DB_G=22 15/16"; DB_H=1 9/16"; DB_J=53 9/16"; DB_R=1 1/8"; E/2=23 3/32"; G+(INLET/2)+1.625"=42 21/32"; G-(INLET/2)-1.625"=4 23/32"; G-(R/2)=3 7/16"; H-J=23 11/16"; INLET=34 15/16"; INLET/2=17 15/32"; INLET/4=8 3/4"; K=1 1/16"; K/2=17/32"; L=24 1/16"; M=48 1/8"; N=4 3/4"; OLD_G=23 11/16"; OLD_R=40 1/2"; OLD_R/2=20 1/4"; P=56 1/8"; S=48 13/16"; S/2=24 13/32"; T=45 7/8"; T/2=22 15/16"; Type Comments=Centrifugal Airfoil Blower Clockwise Down Blast Arrangement 3 Low Profile Class 2; U=7 3/8"; U-N=2 5/8"; V=1"; V+(D-(A+.25"))/2=2 15/32"
- 330_CAF-DWDI_CW_DBD_CLASS_2: ((M+U+U+N+N)-((B+.25")/2))/2=5 1/16"; (A+.25")/2=17 3/8"; (B+.25")/2=23 21/32"; (D-(A+.25"))/2=2"; (INLET/2)+1.5"=20 13/32"; (INLET/2)+1.625"=20 15/32"; (INLET/2)-.125"=18 27/32"; (M-(B+.25")/2=2 15/16"; -(B+.25")/2=-23 21/32"; -P=-60 5/16"; A=34 1/2"; A+.25"=34 3/4"; A/2=17 1/4"; B=47 1/16"; B+.25"=47 5/16"; B/2=23 17/32"; BOTTOM=14 11/32"; C=2 15/16"; C+C=5 7/8"; C/2=1 15/32"; D/2=19 3/8"; D/7=3 7/32"; DB_D=54 11/16"; DB_E=26"; DB_F=62 1/4"; DB_G=25 1/4"; DB_H=2 1/16"; DB_J=57 13/16"; DB_R=1 5/16"; E/2=25 21/32"; G+(INLET/2)+1.625"=46 15/32"; G-(INLET/2)-1.625"=5 17/32"; G-(R/2)=5 7/32"; H-J=26"; INLET=37 15/16"; INLET/2=18 31/32"; INLET/4=9 1/2"; K=1 1/16"; K/2=17/32"; L=26 5/8"; M=53 3/16"; N=4 7/8"; OLD_G=26"; OLD_R=41 9/16"; OLD_R/2=20 25/32"; P=60 5/16"; S=53 3/4"; S/2=26 7/8"; T=50 9/16"; T/2=25 9/32"; Type Comments=Centrifugal Airfoil Blower Clockwise Down Blast Arrangement 3 Low Profile Class 2; U=7"; U-N=2 1/8"; V=1"; V+(D-(A+.25"))/2=3"
- 365_CAF-DWDI_CW_DBD_CLASS_2: ((M+U+U+N+N)-((B+.25")/2))/2=5 1/16"; (A+.25")/2=19 15/32"; (B+.25")/2=26 7/32"; (D-(A+.25"))/2=2"; (INLET/2)+1.5"=22 5/32"; (INLET/2)+1.625"=22 7/32"; (INLET/2)-.125"=20 19/32"; (M-(B+.25")/2=2 15/16"; -(B+.25")/2=-26 7/32"; -P=-65 15/16"; A=38 11/16"; A+.25"=38 15/16"; A/2=19 11/32"; B=52 3/16"; B+.25"=52 7/16"; B/2=26 3/32"; BOTTOM=15 7/8"; C=3 7/16"; C+C=6 7/8"; C/2=1 23/32"; D/2=21 15/32"; D/7=3 19/32"; DB_D=60 1/2"; DB_E=28 3/4"; DB_F=68 5/8"; DB_G=27 15/16"; DB_H=2 1/16"; DB_J=63 3/8"; DB_R=1 5/16"; E/2=28 7/32"; G+(INLET/2)+1.625"=50 31/32"; G-(INLET/2)-1.625"=6 17/32"; G-(R/2)=6 3/32"; H-J=28 3/4"; INLET=41 7/16"; INLET/2=20 23/32"; INLET/4=10 3/8"; K=15/16"; K/2=15/32"; L=29 3/16"; M=58 5/16"; N=5 3/8"; OLD_G=28 3/4"; OLD_R=45 5/16"; OLD_R/2=22 21/32"; P=65 15/16"; S=59 5/16"; S/2=29 21/32"; T=55 11/16"; T/2=27 27/32"; Type Comments=Centrifugal Airfoil Blower Clockwise Down Blast Arrangement 3 Low Profile Class 2; U=7 1/2"; U-N=2 1/8"; V=1"; V+(D-(A+.25"))/2=3"
- 402_CAF-DWDI_CW_DBD_CLASS_2: ((M+U+U+N+N)-((B+.25")/2))/2=5 3/32"; (A+.25")/2=21"; (B+.25")/2=29 1/32"; (D-(A+.25"))/2=2 1/32"; (INLET/2)+1.5"=24 1/32"; (INLET/2)+1.625"=24 3/32"; (INLET/2)-.125"=22 15/32"; (M-(B+.25")/2=3 31/32"; -(B+.25")/2=-29 1/32"; -P=-73"; A=41 3/4"; A+.25"=42"; A/2=20 7/8"; B=57 13/16"; B+.25"=58 1/16"; B/2=28 29/32"; BOTTOM=17 15/32"; C=3 7/16"; C+C=6 7/8"; C/2=1 23/32"; D/2=23 1/32"; D/7=3 27/32"; DB_D=66 5/8"; DB_E=31 5/8"; DB_F=75 7/16"; DB_G=30 3/4"; DB_H=2 1/8"; DB_J=69 1/2"; DB_R=1 3/4"; E/2=31"; G+(INLET/2)+1.625"=55 23/32"; G-(INLET/2)-1.625"=7 17/32"; G-(R/2)=6 25/32"; H-J=31 5/8"; INLET=45 3/16"; INLET/2=22 19/32"; INLET/4=11 5/16"; K=1 1/16"; K/2=17/32"; L=33"; M=66"; N=5 7/8"; OLD_G=31 5/8"; OLD_R=49 11/16"; OLD_R/2=24 27/32"; P=73"; S=64 3/8"; S/2=32 3/16"; T=62 1/2"; T/2=31 1/4"; Type Comments=Centrifugal Airfoil Blower Clockwise Down Blast Arrangement 3 Low Profile Class 2; U=7"; U-N=1 1/8"; V=1 15/16"; V+(D-(A+.25"))/2=3 31/32"
- 445_CAF-DWDI_CW_DBD_CLASS_2: ((M+U+U+N+N)-((B+.25")/2))/2=5 3/32"; (A+.25")/2=23 3/32"; (B+.25")/2=32 1/4"; (D-(A+.25"))/2=2 1/16"; (INLET/2)+1.5"=26 5/32"; (INLET/2)+1.625"=26 7/32"; (INLET/2)-.125"=24 19/32"; (M-(B+.25")/2=3 31/32"; -(B+.25")/2=-32 1/4"; -P=-79 11/16"; A=45 15/16"; A+.25"=46 3/16"; A/2=22 31/32"; B=64 1/4"; B+.25"=64 1/2"; B/2=32 1/8"; BOTTOM=19 11/32"; C=2 7/16"; C+C=4 7/8"; C/2=1 7/32"; D/2=25 5/32"; D/7=4 3/16"; DB_D=73 11/16"; DB_E=35"; DB_F=83 1/4"; DB_G=34 1/16"; DB_H=2 1/8"; DB_J=76 3/16"; DB_R=1 3/4"; E/2=34 9/32"; G+(INLET/2)+1.625"=61 7/32"; G-(INLET/2)-1.625"=8 25/32"; G-(R/2)=8 1/32"; H-J=35"; INLET=49 7/16"; INLET/2=24 23/32"; INLET/4=12 3/8"; K=1 1/16"; K/2=17/32"; L=36 1/4"; M=72 7/16"; N=6 1/8"; OLD_G=35"; OLD_R=53 15/16"; OLD_R/2=26 31/32"; P=79 11/16"; S=71 1/16"; S/2=35 17/32"; T=68 15/16"; T/2=34 15/32"; Type Comments=Centrifugal Airfoil Blower Clockwise Down Blast Arrangement 3 Low Profile Class 2; U=7 1/4"; U-N=1 1/8"; V=1 15/16"; V+(D-(A+.25"))/2=4"
- 490_CAF-DWDI_CW_DBD_CLASS_2: ((M+U+U+N+N)-((B+.25")/2))/2=5 3/32"; (A+.25")/2=25 5/8"; (B+.25")/2=35 3/16"; (D-(A+.25"))/2=2 1/16"; (INLET/2)+1.5"=28 15/16"; (INLET/2)+1.625"=29"; (INLET/2)-.125"=27 3/8"; (M-(B+.25")/2=4 31/32"; -(B+.25")/2=-35 3/16"; -P=-87 15/16"; A=51"; A+.25"=51 1/4"; A/2=25 1/2"; B=70 1/8"; B+.25"=70 3/8"; B/2=35 1/16"; BOTTOM=21 9/32"; C=2 15/16"; C+C=5 7/8"; C/2=1 15/32"; D/2=27 11/16"; D/7=4 5/8"; DB_D=81 1/8"; DB_E=38 9/16"; DB_F=91 7/16"; DB_G=37 1/2"; DB_H=2 1/8"; DB_J=83 7/16"; DB_R=2 1/4"; E/2=37 7/32"; G+(INLET/2)+1.625"=67 9/16"; G-(INLET/2)-1.625"=9 9/16"; G-(R/2)=9 7/32"; H-J=38 9/16"; INLET=55"; INLET/2=27 1/2"; INLET/4=13 3/4"; K=1 1/16"; K/2=17/32"; L=40 3/16"; M=80 5/16"; N=7 1/2"; OLD_G=38 9/16"; OLD_R=58 11/16"; OLD_R/2=29 11/32"; P=87 15/16"; S=77 3/16"; S/2=38 19/32"; T=75 13/16"; T/2=37 29/32"; Type Comments=Centrifugal Airfoil Blower Clockwise Down Blast Arrangement 3 Low Profile Class 2; U=7 5/8"; U-N=1/8"; V=1 15/16"; V+(D-(A+.25"))/2=4"
- 540_CAF-DWDI_CW_DBD_CLASS_2: ((M+U+U+N+N)-((B+.25")/2))/2=6 5/8"; (A+.25")/2=28"; (B+.25")/2=39 3/32"; (D-(A+.25"))/2=2 1/16"; (INLET/2)+1.5"=31 7/16"; (INLET/2)+1.625"=31 1/2"; (INLET/2)-.125"=29 7/8"; (M-(B+.25")/2=5"; -(B+.25")/2=-39 3/32"; -P=-98 11/16"; A=55 3/4"; A+.25"=56"; A/2=27 7/8"; B=77 15/16"; B+.25"=78 3/16"; B/2=38 31/32"; BOTTOM=23 15/32"; C=3 7/16"; C+C=6 7/8"; C/2=1 23/32"; D/2=30 1/16"; D/7=5"; DB_D=89 3/8"; DB_E=42 7/16"; DB_F=101 1/8"; DB_G=41 5/16"; DB_H=2 5/8"; DB_J=91 13/16"; DB_R=2 1/4"; E/2=41 3/32"; G+(INLET/2)+1.625"=73 15/16"; G-(INLET/2)-1.625"=10 15/16"; G-(R/2)=10 19/32"; H-J=42 7/16"; INLET=60"; INLET/2=30"; INLET/4=15"; K=1 1/16"; K/2=17/32"; L=44 1/8"; M=88 3/16"; N=8 7/8"; OLD_G=42 7/16"; OLD_R=63 11/16"; OLD_R/2=31 27/32"; P=98 11/16"; S=85 9/16"; S/2=42 25/32"; T=83 11/16"; T/2=41 27/32"; Type Comments=Centrifugal Airfoil Blower Clockwise Down Blast Arrangement 3 Low Profile Class 2; U=10 1/2"; U-N=1 5/8"; V=1 15/16"; V+(D-(A+.25"))/2=4"
- 600_CAF-DWDI_CW_DBD_CLASS_2: ((M+U+U+N+N)-((B+.25")/2))/2=6 5/8"; (A+.25")/2=31 7/32"; (B+.25")/2=43 1/4"; (D-(A+.25"))/2=2 1/16"; (INLET/2)+1.5"=34 7/16"; (INLET/2)+1.625"=34 1/2"; (INLET/2)-.125"=32 7/8"; (M-(B+.25")/2=6"; -(B+.25")/2=-43 1/4"; -P=-108"; A=62 3/16"; A+.25"=62 7/16"; A/2=31 3/32"; B=86 1/4"; B+.25"=86 1/2"; B/2=43 1/8"; BOTTOM=26 3/32"; C=3 7/16"; C+C=6 7/8"; C/2=1 23/32"; D/2=33 9/32"; D/7=5 9/16"; DB_D=99 5/16"; DB_E=47 1/8"; DB_F=112 1/16"; DB_G=45 15/16"; DB_H=2 5/8"; DB_J=101 7/16"; DB_R=2 3/4"; E/2=45 9/32"; G+(INLET/2)+1.625"=81 5/8"; G-(INLET/2)-1.625"=12 5/8"; G-(R/2)=12 1/8"; H-J=47 1/8"; INLET=66"; INLET/2=33"; INLET/4=16 1/2"; K=1 1/16"; K/2=17/32"; L=49 1/4"; M=98 1/2"; N=8 7/8"; OLD_G=47 1/8"; OLD_R=70"; OLD_R/2=35"; P=108"; S=93 7/8"; S/2=46 15/16"; T=93"; T/2=46 1/2"; Type Comments=Centrifugal Airfoil Blower Clockwise Down Blast Arrangement 3 Low Profile Class 2; U=9 1/2"; U-N=5/8"; V=2 15/16"; V+(D-(A+.25"))/2=5"
- 660_CAF-DWDI_CW_DBD_CLASS_2: ((M+U+U+N+N)-((B+.25")/2))/2=6 5/8"; (A+.25")/2=34 11/32"; (B+.25")/2=47 9/16"; (D-(A+.25"))/2=2 1/16"; (INLET/2)+1.5"=37 7/16"; (INLET/2)+1.625"=37 1/2"; (INLET/2)-.125"=35 7/8"; (M-(B+.25")/2=6"; -(B+.25")/2=-47 9/16"; -P=-116 5/8"; A=68 7/16"; A+.25"=68 11/16"; A/2=34 7/32"; B=94 7/8"; B+.25"=95 1/8"; B/2=47 7/16"; BOTTOM=28 11/16"; C=3 7/16"; C+C=6 7/8"; C/2=1 23/32"; D/2=36 13/32"; D/7=6 1/16"; DB_D=109 3/16"; DB_E=51 13/16"; DB_F=123"; DB_G=50 1/2"; DB_H=2 5/8"; DB_J=110 3/4"; DB_R=2 3/4"; E/2=49 5/8"; G+(INLET/2)+1.625"=89 5/16"; G-(INLET/2)-1.625"=14 5/16"; G-(R/2)=13 17/32"; H-J=51 13/16"; INLET=72"; INLET/2=36"; INLET/4=18"; K=1 1/16"; K/2=17/32"; L=53 9/16"; M=107 1/8"; N=8 7/8"; OLD_G=51 13/16"; OLD_R=76 9/16"; OLD_R/2=38 9/32"; P=116 5/8"; S=103 1/4"; S/2=51 5/8"; T=101 5/8"; T/2=50 13/16"; Type Comments=Centrifugal Airfoil Blower Clockwise Down Blast Arrangement 3 Low Profile Class 2; U=9 1/2"; U-N=5/8"; V=3 15/16"; V+(D-(A+.25"))/2=6"
- 730_CAF-DWDI_CW_DBD_CLASS_2: ((M+U+U+N+N)-((B+.25")/2))/2=6 11/16"; (A+.25")/2=38 1/32"; (B+.25")/2=52 1/2"; (D-(A+.25"))/2=2 9/16"; (INLET/2)+1.5"=40 15/16"; (INLET/2)+1.625"=41"; (INLET/2)-.125"=39 3/8"; (M-(B+.25")/2=6 1/16"; -(B+.25")/2=-52 1/2"; -P=-126 3/4"; A=75 13/16"; A+.25"=76 1/16"; A/2=37 29/32"; B=104 3/4"; B+.25"=105"; B/2=52 3/8"; BOTTOM=31 23/32"; C=3 15/16"; C+C=7 7/8"; C/2=1 31/32"; D/2=40 19/32"; D/7=6 25/32"; DB_D=120 3/4"; DB_E=57 5/16"; DB_F=135 13/16"; DB_G=55 7/8"; DB_H=2 11/16"; DB_J=121 3/4"; DB_R=2 3/4"; E/2=55 1/16"; G+(INLET/2)+1.625"=98 5/16"; G-(INLET/2)-1.625"=16 5/16"; G-(R/2)=15 17/32"; H-J=57 1/4"; INLET=79"; INLET/2=39 1/2"; INLET/4=19 3/4"; K=1 1/16"; K/2=17/32"; L=58 9/16"; M=117 1/8"; N=9"; OLD_G=57 5/16"; OLD_R=83 9/16"; OLD_R/2=41 25/32"; P=126 3/4"; S=114 3/16"; S/2=57 3/32"; T=111 5/8"; T/2=55 13/16"; Type Comments=Centrifugal Airfoil Blower Clockwise Down Blast Arrangement 3 Low Profile Class 2; U=9 5/8"; U-N=5/8"; V=3 7/16"; V+(D-(A+.25"))/2=6"
- 120_CAF-DWDI_CW_DBD_CLASS_3: ((M+U+U+N+N)-((B+.25")/2))/2=3"; (A+.25")/2=6 3/16"; (B+.25")/2=8 31/32"; (D-(A+.25"))/2=15/16"; (INLET/2)+1.5"=9 1/2"; (INLET/2)+1.625"=9 9/16"; (INLET/2)-.125"=7 15/16"; (M-(B+.25")/2=1 15/16"; -(B+.25")/2=-8 31/32"; -P=-31 7/16"; A=12 1/8"; A+.25"=12 3/8"; A/2=6 1/16"; B=17 11/16"; B+.25"=17 15/16"; B/2=8 27/32"; BOTTOM=5 7/32"; C=1 11/16"; C+C=3 3/8"; C/2=27/32"; D/2=7 1/8"; D/7=1 3/16"; DB_D=20 1/16"; DB_E=9 13/16"; DB_F=23 5/16"; DB_G=9 9/16"; DB_H=1 1/16"; DB_J=23 5/16"; DB_R=7/8"; E/2=9 29/32"; G+(INLET/2)+1.625"=19 3/8"; G-(INLET/2)-1.625"=1/4"; G-(R/2)=3/16"; H-J=9 5/8"; INLET=16 1/8"; INLET/2=8 1/16"; INLET/4=4 1/32"; K=15/16"; K/2=15/32"; L=10 15/16"; M=21 13/16"; N=6 1/2"; OLD_G=9 13/16"; OLD_R=19 1/4"; OLD_R/2=9 5/8"; P=31 7/16"; S=20 1/8"; S/2=10 1/16"; T=20 1/16"; T/2=10 1/32"; Type Comments=Centrifugal Airfoil Blower Clockwise Down Blast Arrangement 3 Low Profile Class 3; U=7 9/16"; U-N=1 1/16"; V=1"; V+(D-(A+.25"))/2=1 15/16"
- 135_CAF-DWDI_CW_DBD_CLASS_3: ((M+U+U+N+N)-((B+.25")/2))/2=3"; (A+.25")/2=6 15/16"; (B+.25")/2=10 3/32"; (D-(A+.25"))/2=15/16"; (INLET/2)+1.5"=10 1/4"; (INLET/2)+1.625"=10 5/16"; (INLET/2)-.125"=8 11/16"; (M-(B+.25")/2=1 15/16"; -(B+.25")/2=-10 3/32"; -P=-33 11/16"; A=13 5/8"; A+.25"=13 7/8"; A/2=6 13/16"; B=19 15/16"; B+.25"=20 3/16"; B/2=9 31/32"; BOTTOM=5 7/8"; C=1 15/16"; C+C=3 7/8"; C/2=31/32"; D/2=7 7/8"; D/7=1 5/16"; DB_D=22 9/16"; DB_E=10 13/16"; DB_F=25 3/4"; DB_G=10 7/16"; DB_H=1 1/16"; DB_J=25 3/4"; DB_R=7/8"; E/2=11 1/32"; G+(INLET/2)+1.625"=21 1/8"; G-(INLET/2)-1.625"=1/2"; G-(R/2)=5/16"; H-J=10 13/16"; INLET=17 5/8"; INLET/2=8 13/16"; INLET/4=4 13/32"; K=15/16"; K/2=15/32"; L=12 1/16"; M=24 1/16"; N=6 1/2"; OLD_G=10 13/16"; OLD_R=21"; OLD_R/2=10 1/2"; P=33 11/16"; S=22 5/8"; S/2=11 5/16"; T=22 5/16"; T/2=11 5/32"; Type Comments=Centrifugal Airfoil Blower Clockwise Down Blast Arrangement 3 Low Profile Class 3; U=7 9/16"; U-N=1 1/16"; V=1"; V+(D-(A+.25"))/2=1 15/16"
- 150_CAF-DWDI_CW_DBD_CLASS_3: ((M+U+U+N+N)-((B+.25")/2))/2=3"; (A+.25")/2=7 3/4"; (B+.25")/2=11 1/8"; (D-(A+.25"))/2=15/16"; (INLET/2)+1.5"=11"; (INLET/2)+1.625"=11 1/16"; (INLET/2)-.125"=9 7/16"; (M-(B+.25")/2=1 15/16"; -(B+.25")/2=-11 1/8"; -P=-35 3/4"; A=15 1/4"; A+.25"=15 1/2"; A/2=7 5/8"; B=22"; B+.25"=22 1/4"; B/2=11"; BOTTOM=6 17/32"; C=1 15/16"; C+C=3 7/8"; C/2=31/32"; D/2=8 11/16"; D/7=1 7/16"; DB_D=25 1/16"; DB_E=12"; DB_F=28 7/16"; DB_G=11 1/2"; DB_H=1 1/16"; DB_J=28 1/8"; DB_R=7/8"; E/2=12 1/16"; G+(INLET/2)+1.625"=23 1/16"; G-(INLET/2)-1.625"=15/16"; G-(R/2)=3/4"; H-J=12"; INLET=19 1/8"; INLET/2=9 9/16"; INLET/4=4 25/32"; K=15/16"; K/2=15/32"; L=13 1/16"; M=26 1/8"; N=6 1/2"; OLD_G=12"; OLD_R=22 1/2"; OLD_R/2=11 1/4"; P=35 3/4"; S=24 15/16"; S/2=12 15/32"; T=24 3/8"; T/2=12 3/16"; Type Comments=Centrifugal Airfoil Blower Clockwise Down Blast Arrangement 3 Low Profile Class 3; U=7 9/16"; U-N=1 1/16"; V=1"; V+(D-(A+.25"))/2=1 15/16"
- 165_CAF-DWDI_CW_DBD_CLASS_3: ((M+U+U+N+N)-((B+.25")/2))/2=3 1/2"; (A+.25")/2=8 19/32"; (B+.25")/2=12 1/8"; (D-(A+.25"))/2=15/16"; (INLET/2)+1.5"=12 1/32"; (INLET/2)+1.625"=12 3/32"; (INLET/2)-.125"=10 15/32"; (M-(B+.25")/2=1 15/16"; -(B+.25")/2=-12 1/8"; -P=-38 5/16"; A=16 15/16"; A+.25"=17 3/16"; A/2=8 15/32"; B=24"; B+.25"=24 1/4"; B/2=12"; BOTTOM=7 3/16"; C=2 3/16"; C+C=4 3/8"; C/2=1 3/32"; D/2=9 17/32"; D/7=1 19/32"; DB_D=27 1/2"; DB_E=13 1/8"; DB_F=31 3/16"; DB_G=12 11/16"; DB_H=1 1/16"; DB_J=30 9/16"; DB_R=7/8"; E/2=13 1/16"; G+(INLET/2)+1.625"=25 7/32"; G-(INLET/2)-1.625"=1 1/32"; G-(R/2)=1"; H-J=13 1/8"; INLET=21 3/16"; INLET/2=10 19/32"; INLET/4=5 5/16"; K=15/16"; K/2=15/32"; L=14 1/16"; M=28 1/8"; N=6 1/2"; OLD_G=13 1/8"; OLD_R=24 1/4"; OLD_R/2=12 1/8"; P=38 5/16"; S=27 3/8"; S/2=13 11/16"; T=26 3/8"; T/2=13 3/16"; Type Comments=Centrifugal Airfoil Blower Clockwise Down Blast Arrangement 3 Low Profile Class 3; U=8 1/16"; U-N=1 9/16"; V=1"; V+(D-(A+.25"))/2=1 15/16"
- 180_CAF-DWDI_CW_DBD_CLASS_3: ((M+U+U+N+N)-((B+.25")/2))/2=3 1/2"; (A+.25")/2=9 3/8"; (B+.25")/2=13 5/32"; (D-(A+.25"))/2=15/16"; (INLET/2)+1.5"=12 25/32"; (INLET/2)+1.625"=12 27/32"; (INLET/2)-.125"=11 7/32"; (M-(B+.25")/2=1 15/16"; -(B+.25")/2=-13 5/32"; -P=-40 3/8"; A=18 1/2"; A+.25"=18 3/4"; A/2=9 1/4"; B=26 1/16"; B+.25"=26 5/16"; B/2=13 1/32"; BOTTOM=7 27/32"; C=2 3/16"; C+C=4 3/8"; C/2=1 3/32"; D/2=10 5/16"; D/7=1 23/32"; DB_D=30"; DB_E=14 5/16"; DB_F=33 15/16"; DB_G=13 13/16"; DB_H=1 1/16"; DB_J=32 7/8"; DB_R=7/8"; E/2=14 3/32"; G+(INLET/2)+1.625"=27 5/32"; G-(INLET/2)-1.625"=1 15/32"; G-(R/2)=15/16"; H-J=14 5/16"; INLET=22 11/16"; INLET/2=11 11/32"; INLET/4=5 11/16"; K=15/16"; K/2=15/32"; L=15 1/8"; M=30 3/16"; N=6 1/2"; OLD_G=14 5/16"; OLD_R=26 3/4"; OLD_R/2=13 3/8"; P=40 3/8"; S=29 3/4"; S/2=14 7/8"; T=28 7/16"; T/2=14 7/32"; Type Comments=Centrifugal Airfoil Blower Clockwise Down Blast Arrangement 3 Low Profile Class 3; U=8 1/16"; U-N=1 9/16"; V=1"; V+(D-(A+.25"))/2=1 15/16"
- 195_CAF-DWDI_CW_DBD_CLASS_3: ((M+U+U+N+N)-((B+.25")/2))/2=4"; (A+.25")/2=9 7/8"; (B+.25")/2=14 11/32"; (D-(A+.25"))/2=31/32"; (INLET/2)+1.5"=13 17/32"; (INLET/2)+1.625"=13 19/32"; (INLET/2)-.125"=11 31/32"; (M-(B+.25")/2=2 7/16"; -(B+.25")/2=-14 11/32"; -P=-42 3/4"; A=19 1/2"; A+.25"=19 3/4"; A/2=9 3/4"; B=28 7/16"; B+.25"=28 11/16"; B/2=14 7/32"; BOTTOM=8 15/32"; C=2 3/16"; C+C=4 3/8"; C/2=1 3/32"; D/2=10 27/32"; D/7=1 13/16"; DB_D=32 7/16"; DB_E=15 1/2"; DB_F=37 11/16"; DB_G=14 15/16"; DB_H=2 1/16"; DB_J=36 3/8"; DB_R=7/8"; E/2=15 5/16"; G+(INLET/2)+1.625"=29 3/32"; G-(INLET/2)-1.625"=1 29/32"; G-(R/2)=1 1/4"; H-J=15 1/2"; INLET=24 3/16"; INLET/2=12 3/32"; INLET/4=6 1/16"; K=15/16"; K/2=15/32"; L=16 13/16"; M=33 9/16"; N=6 1/2"; OLD_G=15 1/2"; OLD_R=28 1/2"; OLD_R/2=14 1/4"; P=42 3/4"; S=32 11/16"; S/2=16 11/32"; T=31 5/16"; T/2=15 21/32"; Type Comments=Centrifugal Airfoil Blower Clockwise Down Blast Arrangement 3 Low Profile Class 3; U=8 1/16"; U-N=1 9/16"; V=1"; V+(D-(A+.25"))/2=1 31/32"
- 210_CAF-DWDI_CW_DBD_CLASS_3: ((M+U+U+N+N)-((B+.25")/2))/2=4"; (A+.25")/2=10 15/16"; (B+.25")/2=15 5/16"; (D-(A+.25"))/2=31/32"; (INLET/2)+1.5"=14 13/32"; (INLET/2)+1.625"=14 15/32"; (INLET/2)-.125"=12 27/32"; (M-(B+.25")/2=2 7/16"; -(B+.25")/2=-15 5/16"; -P=-45 3/16"; A=21 5/8"; A+.25"=21 7/8"; A/2=10 13/16"; B=30 3/8"; B+.25"=30 5/8"; B/2=15 3/16"; BOTTOM=9 1/8"; C=2 3/16"; C+C=4 3/8"; C/2=1 3/32"; D/2=11 29/32"; D/7=2"; DB_D=34 15/16"; DB_E=16 11/16"; DB_F=40 3/8"; DB_G=16 1/8"; DB_H=2 1/16"; DB_J=38 11/16"; DB_R=1 1/8"; E/2=16 9/32"; G+(INLET/2)+1.625"=31 5/32"; G-(INLET/2)-1.625"=2 7/32"; G-(R/2)=1 11/16"; H-J=16 11/16"; INLET=25 15/16"; INLET/2=12 31/32"; INLET/4=6 1/2"; K=15/16"; K/2=15/32"; L=17 3/4"; M=35 1/2"; N=7"; OLD_G=16 11/16"; OLD_R=30"; OLD_R/2=15"; P=45 3/16"; S=35 1/16"; S/2=17 17/32"; T=33 1/4"; T/2=16 5/8"; Type Comments=Centrifugal Airfoil Blower Clockwise Down Blast Arrangement 3 Low Profile Class 3; U=8 9/16"; U-N=1 9/16"; V=1"; V+(D-(A+.25"))/2=1 31/32"
- 225_CAF-DWDI_CW_DBD_CLASS_3: ((M+U+U+N+N)-((B+.25")/2))/2=4"; (A+.25")/2=11 23/32"; (B+.25")/2=16 3/8"; (D-(A+.25"))/2=1 15/32"; (INLET/2)+1.5"=15 5/32"; (INLET/2)+1.625"=15 7/32"; (INLET/2)-.125"=13 19/32"; (M-(B+.25")/2=2 7/16"; -(B+.25")/2=-16 3/8"; -P=-47 5/16"; A=23 3/16"; A+.25"=23 7/16"; A/2=11 19/32"; B=32 1/2"; B+.25"=32 3/4"; B/2=16 1/4"; BOTTOM=9 25/32"; C=2 3/16"; C+C=4 3/8"; C/2=1 3/32"; D/2=13 3/16"; D/7=2 3/16"; DB_D=37 7/16"; DB_E=17 13/16"; DB_F=43 1/8"; DB_G=17 1/4"; DB_H=2 1/16"; DB_J=41 3/16"; DB_R=1 1/8"; E/2=17 27/32"; G+(INLET/2)+1.625"=33 1/32"; G-(INLET/2)-1.625"=2 19/32"; G-(R/2)=1 15/16"; H-J=17 13/16"; INLET=27 7/16"; INLET/2=13 23/32"; INLET/4=6 7/8"; K=15/16"; K/2=15/32"; L=18 13/16"; M=37 5/8"; N=7"; OLD_G=17 13/16"; OLD_R=31 3/4"; OLD_R/2=15 7/8"; P=47 5/16"; S=37 1/2"; S/2=18 3/4"; T=35 3/8"; T/2=17 11/16"; Type Comments=Centrifugal Airfoil Blower Clockwise Down Blast Arrangement 3 Low Profile Class 3; U=8 9/16"; U-N=1 9/16"; V=1"; V+(D-(A+.25"))/2=2 15/32"
- 245_CAF-DWDI_CW_DBD_CLASS_3: ((M+U+U+N+N)-((B+.25")/2))/2=3 1/2"; (A+.25")/2=12 7/8"; (B+.25")/2=17 21/32"; (D-(A+.25"))/2=1 15/32"; (INLET/2)+1.5"=16 5/32"; (INLET/2)+1.625"=16 7/32"; (INLET/2)-.125"=14 19/32"; (M-(B+.25")/2=2 15/16"; -(B+.25")/2=-17 21/32"; -P=-50 13/16"; A=25 1/2"; A+.25"=25 3/4"; A/2=12 3/4"; B=35 1/16"; B+.25"=35 5/16"; B/2=17 17/32"; BOTTOM=10 21/32"; C=2 7/16"; C+C=4 7/8"; C/2=1 7/32"; D/2=14 11/32"; D/7=2 13/32"; DB_D=40 11/16"; DB_E=19 3/8"; DB_F=46 3/4"; DB_G=18 3/4"; DB_H=2 1/16"; DB_J=44 7/16"; DB_R=1 5/16"; E/2=19 1/8"; G+(INLET/2)+1.625"=35 19/32"; G-(INLET/2)-1.625"=3 5/32"; G-(R/2)=2 1/2"; H-J=19 3/8"; INLET=29 7/16"; INLET/2=14 23/32"; INLET/4=7 3/8"; K=1 1/16"; K/2=17/32"; L=20 5/8"; M=41 3/16"; N=7"; OLD_G=19 3/8"; OLD_R=33 3/4"; OLD_R/2=16 7/8"; P=50 13/16"; S=40 1/4"; S/2=20 1/8"; T=38 9/16"; T/2=19 9/32"; Type Comments=Centrifugal Airfoil Blower Clockwise Down Blast Arrangement 3 Low Profile Class 3; U=7 9/16"; U-N=9/16"; V=1"; V+(D-(A+.25"))/2=2 15/32"
- 270_CAF-DWDI_CW_DBD_CLASS_3: ((M+U+U+N+N)-((B+.25")/2))/2=3 1/2"; (A+.25")/2=13 7/8"; (B+.25")/2=19 27/32"; (D-(A+.25"))/2=1 15/32"; (INLET/2)+1.5"=17 13/32"; (INLET/2)+1.625"=17 15/32"; (INLET/2)-.125"=15 27/32"; (M-(B+.25")/2=2 15/16"; -(B+.25")/2=-19 27/32"; -P=-55 5/16"; A=27 1/2"; A+.25"=27 3/4"; A/2=13 3/4"; B=39 7/16"; B+.25"=39 11/16"; B/2=19 23/32"; BOTTOM=11 3/4"; C=2 7/16"; C+C=4 7/8"; C/2=1 7/32"; D/2=15 11/32"; D/7=2 9/16"; DB_D=44 13/16"; DB_E=21 5/16"; DB_F=51 5/16"; DB_G=20 11/16"; DB_H=2 1/16"; DB_J=48 1/2"; DB_R=1 5/16"; E/2=21 5/16"; G+(INLET/2)+1.625"=38 25/32"; G-(INLET/2)-1.625"=3 27/32"; G-(R/2)=2 9/16"; H-J=21 5/16"; INLET=31 15/16"; INLET/2=15 31/32"; INLET/4=8"; K=1 1/16"; K/2=17/32"; L=22 13/16"; M=45 9/16"; N=7 1/8"; OLD_G=21 5/16"; OLD_R=37 1/2"; OLD_R/2=18 3/4"; P=55 5/16"; S=44 1/4"; S/2=22 1/8"; T=42 15/16"; T/2=21 15/32"; Type Comments=Centrifugal Airfoil Blower Clockwise Down Blast Arrangement 3 Low Profile Class 3; U=7 11/16"; U-N=9/16"; V=1"; V+(D-(A+.25"))/2=2 15/32"
- 300_CAF-DWDI_CW_DBD_CLASS_3: ((M+U+U+N+N)-((B+.25")/2))/2=3 9/16"; (A+.25")/2=15 23/32"; (B+.25")/2=21 5/8"; (D-(A+.25"))/2=1 15/32"; (INLET/2)+1.5"=18 29/32"; (INLET/2)+1.625"=18 31/32"; (INLET/2)-.125"=17 11/32"; (M-(B+.25")/2=2 15/16"; -(B+.25")/2=-21 5/8"; -P=-58 7/8"; A=31 3/16"; A+.25"=31 7/16"; A/2=15 19/32"; B=43"; B+.25"=43 1/4"; B/2=21 1/2"; BOTTOM=13 1/32"; C=2 7/16"; C+C=4 7/8"; C/2=1 7/32"; D/2=17 3/16"; D/7=2 7/8"; DB_D=49 3/4"; DB_E=23 11/16"; DB_F=56 13/16"; DB_G=22 15/16"; DB_H=2 1/16"; DB_J=53 3/16"; DB_R=1 1/8"; E/2=1 5/16"; G+(INLET/2)+1.625"=42 21/32"; G-(INLET/2)-1.625"=4 23/32"; G-(R/2)=3 7/16"; H-J=23 11/16"; INLET=34 15/16"; INLET/2=17 15/32"; INLET/4=8 3/4"; K=1 1/16"; K/2=17/32"; L=24 9/16"; M=49 1/8"; N=7 1/8"; OLD_G=23 11/16"; OLD_R=40 1/2"; OLD_R/2=20 1/4"; P=58 7/8"; S=48 15/16"; S/2=24 15/32"; T=46 1/2"; T/2=23 1/4"; Type Comments=Centrifugal Airfoil Blower Clockwise Down Blast Arrangement 3 Low Profile Class 3; U=7 3/4"; U-N=5/8"; V=1"; V+(D-(A+.25"))/2=2 15/32"
- 330_CAF-DWDI_CW_DBD_CLASS_3: ((M+U+U+N+N)-((B+.25")/2))/2=3 19/32"; (A+.25")/2=17 3/8"; (B+.25")/2=23 21/32"; (D-(A+.25"))/2=2"; (INLET/2)+1.5"=20 13/32"; (INLET/2)+1.625"=20 15/32"; (INLET/2)-.125"=18 27/32"; (M-(B+.25")/2=3 31/32"; -(B+.25")/2=-23 21/32"; -P=-64"; A=34 1/2"; A+.25"=34 3/4"; A/2=17 1/4"; B=47 1/16"; B+.25"=47 5/16"; B/2=23 17/32"; BOTTOM=14 11/32"; C=2 7/16"; C+C=4 7/8"; C/2=1 7/32"; D/2=19 3/8"; D/7=3 7/32"; DB_D=54 3/4"; DB_E=26 1/16"; DB_F=62 5/16"; DB_G=25 5/16"; DB_H=2 1/8"; DB_J=58 3/16"; DB_R=1 5/16"; E/2=25 21/32"; G+(INLET/2)+1.625"=46 17/32"; G-(INLET/2)-1.625"=5 19/32"; G-(R/2)=5 9/32"; H-J=26"; INLET=37 15/16"; INLET/2=18 31/32"; INLET/4=9 1/2"; K=1 1/16"; K/2=17/32"; L=27 5/8"; M=55 1/4"; N=7 1/8"; OLD_G=26 1/16"; OLD_R=41 9/16"; OLD_R/2=20 25/32"; P=64"; S=52 15/16"; S/2=26 15/32"; T=51 3/4"; T/2=25 7/8"; Type Comments=Centrifugal Airfoil Blower Clockwise Down Blast Arrangement 3 Low Profile Class 3; U=6 3/4"; U-N=-3/8"; V=1"; V+(D-(A+.25"))/2=3"
- 365_CAF-DWDI_CW_DBD_CLASS_3: ((M+U+U+N+N)-((B+.25")/2))/2=4 3/32"; (A+.25")/2=19 15/32"; (B+.25")/2=26 7/32"; (D-(A+.25"))/2=2"; (INLET/2)+1.5"=22 5/32"; (INLET/2)+1.625"=22 7/32"; (INLET/2)-.125"=20 19/32"; (M-(B+.25")/2=3 31/32"; -(B+.25")/2=-26 7/32"; -P=-70 1/8"; A=38 11/16"; A+.25"=38 15/16"; A/2=19 11/32"; B=52 3/16"; B+.25"=52 7/16"; B/2=26 3/32"; BOTTOM=15 7/8"; C=2 15/16"; C+C=5 7/8"; C/2=1 15/32"; D/2=21 15/32"; D/7=3 19/32"; DB_D=60 1/2"; DB_E=28 3/4"; DB_F=69 3/16"; DB_G=27 15/16"; DB_H=2 5/8"; DB_J=64 1/4"; DB_R=1 3/4"; E/2=28 7/32"; G+(INLET/2)+1.625"=50 31/32"; G-(INLET/2)-1.625"=6 17/32"; G-(R/2)=6 3/32"; H-J=28 3/4"; INLET=41 7/16"; INLET/2=20 23/32"; INLET/4=10 3/8"; K=1 1/16"; K/2=17/32"; L=30 3/16"; M=60 3/8"; N=7 5/8"; OLD_G=28 3/4"; OLD_R=45 5/16"; OLD_R/2=22 21/32"; P=70 1/8"; S=59"; S/2=29 1/2"; T=56 7/8"; T/2=28 7/16"; Type Comments=Centrifugal Airfoil Blower Clockwise Down Blast Arrangement 3 Low Profile Class 3; U=7 3/4"; U-N=1/8"; V=1"; V+(D-(A+.25"))/2=3"
- 402_CAF-DWDI_CW_DBD_CLASS_3: ((M+U+U+N+N)-((B+.25")/2))/2=5 19/32"; (A+.25")/2=21"; (B+.25")/2=29 1/32"; (D-(A+.25"))/2=2 1/32"; (INLET/2)+1.5"=24 1/32"; (INLET/2)+1.625"=24 3/32"; (INLET/2)-.125"=22 15/32"; (M-(B+.25")/2=4 31/32"; -(B+.25")/2=-29 1/32"; -P=-80 3/4"; A=41 3/4"; A+.25"=42"; A/2=20 7/8"; B=57 13/16"; B+.25"=58 1/16"; B/2=28 29/32"; BOTTOM=17 15/32"; C=3 7/16"; C+C=6 7/8"; C/2=1 23/32"; D/2=23 1/32"; D/7=3 27/32"; DB_D=66 5/8"; DB_E=31 5/8"; DB_F=75 15/16"; DB_G=30 3/4"; DB_H=2 5/8"; DB_J=70 7/16"; DB_R=2 1/4"; E/2=31"; G+(INLET/2)+1.625"=55 23/32"; G-(INLET/2)-1.625"=7 17/32"; G-(R/2)=6 25/32"; H-J=31 5/8"; INLET=45 3/16"; INLET/2=22 19/32"; INLET/4=11 5/16"; K=1 1/16"; K/2=17/32"; L=34"; M=68"; N=10 1/8"; OLD_G=31 5/8"; OLD_R=49 11/16"; OLD_R/2=24 27/32"; P=80 3/4"; S=63 7/8"; S/2=31 15/16"; T=63 1/2"; T/2=31 3/4"; Type Comments=Centrifugal Airfoil Blower Clockwise Down Blast Arrangement 3 Low Profile Class 3; U=10 3/4"; U-N=5/8"; V=1 15/16"; V+(D-(A+.25"))/2=3 31/32"
- 445_CAF-DWDI_CW_DBD_CLASS_3: ((M+U+U+N+N)-((B+.25")/2))/2=5 5/8"; (A+.25")/2=23 3/32"; (B+.25")/2=32 1/4"; (D-(A+.25"))/2=2 1/16"; (INLET/2)+1.5"=26 5/32"; (INLET/2)+1.625"=26 7/32"; (INLET/2)-.125"=24 19/32"; (M-(B+.25")/2=5"; -(B+.25")/2=-32 1/4"; -P=-87 1/4"; A=45 15/16"; A+.25"=46 3/16"; A/2=22 31/32"; B=64 1/4"; B+.25"=64 1/2"; B/2=32 1/8"; BOTTOM=19 11/32"; C=3 7/16"; C+C=6 7/8"; C/2=1 23/32"; D/2=25 5/32"; D/7=4 3/16"; DB_D=73 3/4"; DB_E=35"; DB_F=83 13/16"; DB_G=34 1/16"; DB_H=2 5/8"; DB_J=77 1/8"; DB_R=2 1/4"; E/2=34 9/32"; G+(INLET/2)+1.625"=61 7/32"; G-(INLET/2)-1.625"=8 25/32"; G-(R/2)=8 1/32"; H-J=35"; INLET=49 7/16"; INLET/2=24 23/32"; INLET/4=12 3/8"; K=1 1/16"; K/2=17/32"; L=37 1/4"; M=74 1/2"; N=10 1/8"; OLD_G=35"; OLD_R=53 15/16"; OLD_R/2=26 31/32"; P=87 1/4"; S=70 5/8"; S/2=35 5/16"; T=70"; T/2=35"; Type Comments=Centrifugal Airfoil Blower Clockwise Down Blast Arrangement 3 Low Profile Class 3; U=10 3/4"; U-N=5/8"; V=1 15/16"; V+(D-(A+.25"))/2=4"
- 490_CAF-DWDI_CW_DBD_CLASS_3: ((M+U+U+N+N)-((B+.25")/2))/2=4 5/8"; (A+.25")/2=25 5/8"; (B+.25")/2=35 3/16"; (D-(A+.25"))/2=2 1/16"; (INLET/2)+1.5"=28 15/16"; (INLET/2)+1.625"=29"; (INLET/2)-.125"=27 3/8"; (M-(B+.25")/2=6"; -(B+.25")/2=-35 3/16"; -P=-98 1/2"; A=51"; A+.25"=51 1/4"; A/2=25 1/2"; B=70 1/8"; B+.25"=70 3/8"; B/2=35 1/16"; BOTTOM=21 9/32"; C=3 15/16"; C+C=7 7/8"; C/2=1 31/32"; D/2=27 11/16"; D/7=4 5/8"; DB_D=81 1/8"; DB_E=38 9/16"; DB_F=92"; DB_G=37 1/2"; DB_H=2 5/8"; DB_J=84 1/2"; DB_R=2 3/4"; E/2=37 7/32"; G+(INLET/2)+1.625"=67 9/16"; G-(INLET/2)-1.625"=9 9/16"; G-(R/2)=9 7/32"; H-J=38 9/16"; INLET=55"; INLET/2=27 1/2"; INLET/4=13 3/4"; K=1 1/16"; K/2=17/32"; L=41 3/16"; M=82 3/8"; N=13 1/2"; OLD_G=38 9/16"; OLD_R=58 11/16"; OLD_R/2=29 11/32"; P=98 1/2"; S=76 3/4"; S/2=38 3/8"; T=76 7/8"; T/2=38 7/16"; Type Comments=Centrifugal Airfoil Blower Clockwise Down Blast Arrangement 3 Low Profile Class 3; U=12 1/8"; U-N=-1 3/8"; V=1 15/16"; V+(D-(A+.25"))/2=4"
- 540_CAF-DWDI_CW_DBD_CLASS_3: ((M+U+U+N+N)-((B+.25")/2))/2=6 11/16"; (A+.25")/2=28"; (B+.25")/2=39 3/32"; (D-(A+.25"))/2=2 1/16"; (INLET/2)+1.5"=31 7/16"; (INLET/2)+1.625"=31 1/2"; (INLET/2)-.125"=29 7/8"; (M-(B+.25")/2=6 1/16"; -(B+.25")/2=-39 3/32"; -P=-110 11/16"; A=55 3/4"; A+.25"=56"; A/2=27 7/8"; B=77 15/16"; B+.25"=78 3/16"; B/2=38 31/32"; BOTTOM=23 15/32"; C=4 7/16"; C+C=8 7/8"; C/2=2 7/32"; D/2=30 1/16"; D/7=5"; DB_D=89 7/16"; DB_E=42 7/16"; DB_F=101 3/16"; DB_G=41 3/8"; DB_H=2 11/16"; DB_J=92 5/16"; DB_R=2 3/4"; E/2=41 3/32"; G+(INLET/2)+1.625"=73 15/16"; G-(INLET/2)-1.625"=10 15/16"; G-(R/2)=10 19/32"; H-J=42 7/16"; INLET=60"; INLET/2=30"; INLET/4=15"; K=1 3/16"; K/2=19/32"; L=45 1/8"; M=90 5/16"; N=15 3/4"; OLD_G=42 7/16"; OLD_R=63 11/16"; OLD_R/2=31 27/32"; P=110 11/16"; S=84 9/16"; S/2=42 9/32"; T=84 13/16"; T/2=42 13/32"; Type Comments=Centrifugal Airfoil Blower Clockwise Down Blast Arrangement 3 Low Profile Class 3; U=16 3/8"; U-N=5/8"; V=1 15/16"; V+(D-(A+.25"))/2=4"
- 600_CAF-DWDI_CW_DBD_CLASS_3: ((M+U+U+N+N)-((B+.25")/2))/2=6 3/16"; (A+.25")/2=31 7/32"; (B+.25")/2=43 1/4"; (D-(A+.25"))/2=2 1/16"; (INLET/2)+1.5"=34 7/16"; (INLET/2)+1.625"=34 1/2"; (INLET/2)-.125"=32 7/8"; (M-(B+.25")/2=6 1/16"; -(B+.25")/2=-43 1/4"; -P=-118 5/8"; A=62 3/16"; A+.25"=62 7/16"; A/2=31 3/32"; B=86 1/4"; B+.25"=86 1/2"; B/2=43 1/8"; BOTTOM=26 3/32"; C=4 15/16"; C+C=9 7/8"; C/2=2 15/32"; D/2=33 9/32"; D/7=5 9/16"; DB_D=99 5/16"; DB_E=47 1/8"; DB_F=112 1/8"; DB_G=45 15/16"; DB_H=2 11/16"; DB_J=101 11/16"; DB_R=2 3/4"; E/2=45 9/32"; G+(INLET/2)+1.625"=81 5/8"; G-(INLET/2)-1.625"=12 5/8"; G-(R/2)=12 1/8"; H-J=47 1/8"; INLET=66"; INLET/2=33"; INLET/4=16 1/2"; K=1 3/16"; K/2=19/32"; L=49 5/16"; M=98 5/8"; N=15 7/8"; OLD_G=47 1/8"; OLD_R=70"; OLD_R/2=35"; P=118 5/8"; S=93 15/16"; S/2=46 31/32"; T=93 1/8"; T/2=46 9/16"; Type Comments=Centrifugal Airfoil Blower Clockwise Down Blast Arrangement 3 Low Profile Class 3; U=16"; U-N=1/8"; V=2 15/16"; V+(D-(A+.25"))/2=5"

## geometry (parser evidence)
native form markers: Sweep x3
no freeform markers — native parametric forms only
